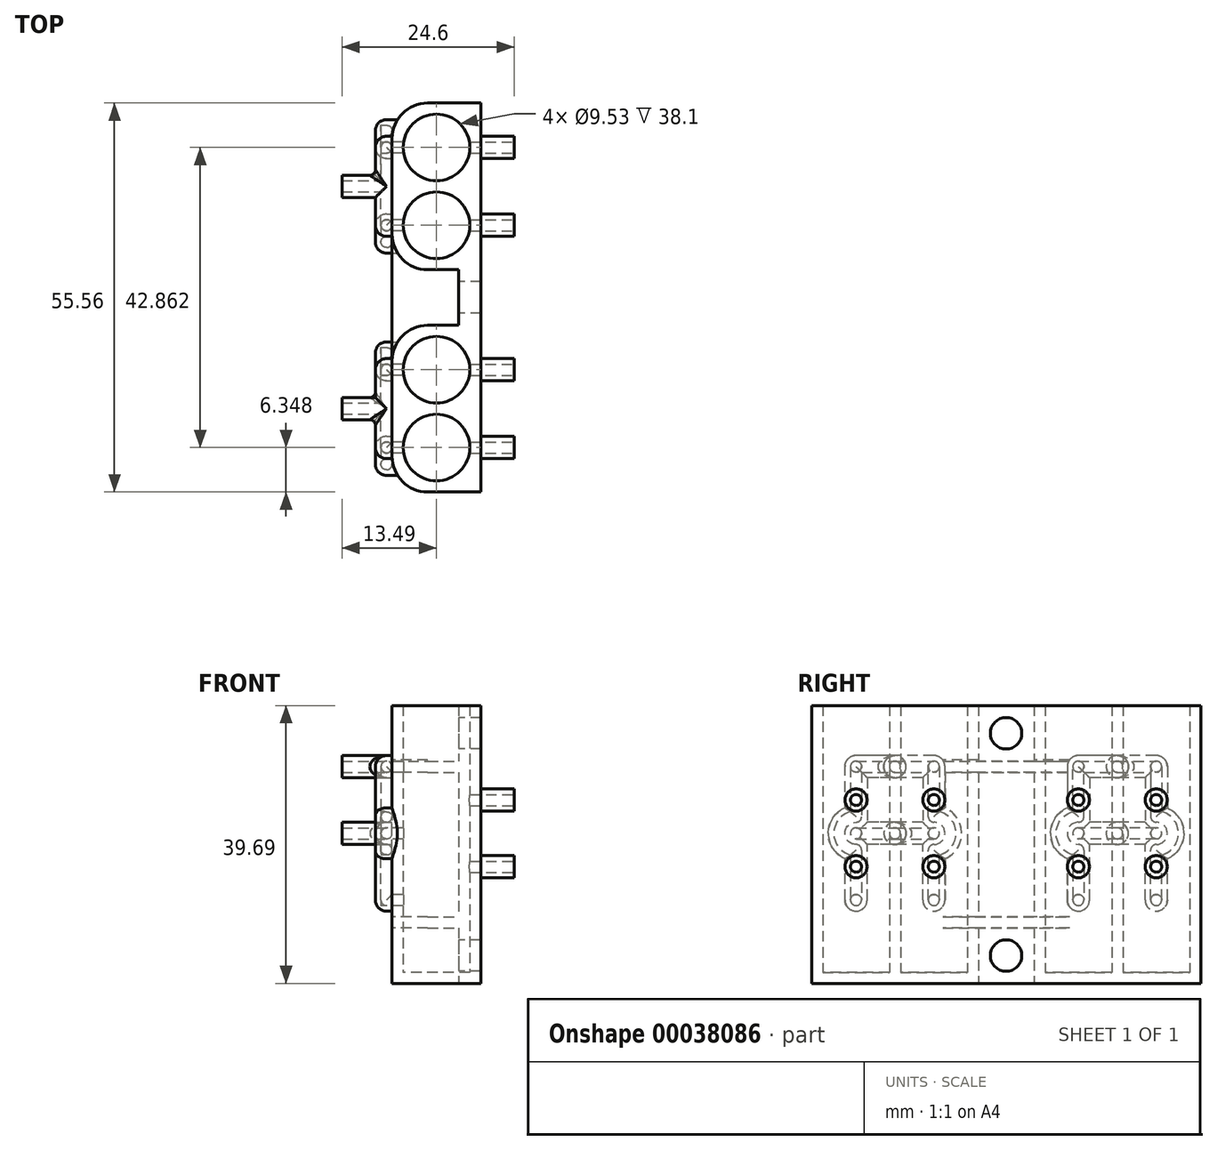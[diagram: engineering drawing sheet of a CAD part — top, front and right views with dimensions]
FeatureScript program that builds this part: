
annotation { "Feature Type Name" : "Feature", "Feature Type Description" : "" }
export const myFeature = defineFeature(function(context is Context, id is Id, definition is map)
    precondition{}
    {
        {
            var Q0;
            Q0=qCreatedBy(makeId("Top.planeOp"),FACE);
            var sketch = newSketch(context, id + "F0", { "sketchPlane" : qUnion([Q0])});
            skLineSegment(sketch, "E0.bottom", {"start": v(0, 0) * mm, "end": v(12.7, 0) * mm});
            skLineSegment(sketch, "E0.top", {"start": v(0, -23.81) * mm, "end": v(9.53, -23.81) * mm});
            skLineSegment(sketch, "E0.left", {"start": v(0, 0) * mm, "end": v(0, -23.81) * mm});
            skLineSegment(sketch, "E0.right", {"start": v(12.7, 0) * mm, "end": v(12.7, -55.56) * mm});
            skLineSegment(sketch, "E1", {"start": v(6.35, 0) * mm, "end": v(6.35, -6.35) * mm, "construction": true});
            skLineSegment(sketch, "E2", {"start": v(6.35, -6.35) * mm, "end": v(6.35, -17.46) * mm, "construction": true});
            skLineSegment(sketch, "E3", {"start": v(6.35, -17.46) * mm, "end": v(6.35, -23.81) * mm, "construction": true});
            skCircle(sketch, "E4", {"center": v(6.35, -17.46) * mm, "radius": 4.76 * mm});
            skCircle(sketch, "E5", {"center": v(6.35, -6.35) * mm, "radius": 4.76 * mm});
            skLineSegment(sketch, "E6", {"start": v(9.53, -23.81) * mm, "end": v(9.53, -31.75) * mm});
            skLineSegment(sketch, "E7.bottom", {"start": v(9.53, -31.75) * mm, "end": v(0, -31.75) * mm});
            skLineSegment(sketch, "E7.top", {"start": v(12.7, -55.56) * mm, "end": v(0, -55.56) * mm});
            skLineSegment(sketch, "E7.right", {"start": v(0, -31.75) * mm, "end": v(0, -55.56) * mm});
            skLineSegment(sketch, "E8", {"start": v(9.53, -27.78) * mm, "end": v(12.7, -27.78) * mm, "construction": true});
            skLineSegment(sketch, "E9", {"start": v(6.35, -31.75) * mm, "end": v(6.35, -38.1) * mm, "construction": true});
            skLineSegment(sketch, "E10", {"start": v(6.35, -38.1) * mm, "end": v(6.35, -49.21) * mm, "construction": true});
            skLineSegment(sketch, "E11", {"start": v(6.35, -49.21) * mm, "end": v(6.35, -55.56) * mm, "construction": true});
            skCircle(sketch, "E12", {"center": v(6.35, -49.21) * mm, "radius": 4.76 * mm});
            skCircle(sketch, "E13", {"center": v(6.35, -38.1) * mm, "radius": 4.76 * mm});
            skSolve(sketch);
        }
        {
            var Q0;
            Q0 = qSketchRegion(id + "F0", true);
            extrude(context, id + "F1", {"entities" : qUnion([Q0]), "depth" : 31.75 * mm});
        }
        {
            var Q0;
            Q0=makeQuery(id+"F1.opExtrude","SWEPT_FACE",FACE,{"disambiguationData":[OSD([sQuery(id+"F0.wireOp",EDGE,"E0.left")])]});
            var sketch = newSketch(context, id + "F2", { "sketchPlane" : qUnion([Q0])});
            skLineSegment(sketch, "E14", {"start": v(17.46, 31.75) * mm, "end": v(17.46, 29.37) * mm, "construction": true});
            skLineSegment(sketch, "E15", {"start": v(6.35, 31.75) * mm, "end": v(6.35, 29.37) * mm, "construction": true});
            skLineSegment(sketch, "E16", {"start": v(17.46, 29.37) * mm, "end": v(17.46, 19.84) * mm, "construction": true});
            skLineSegment(sketch, "E17", {"start": v(17.46, 19.84) * mm, "end": v(17.46, 10.32) * mm, "construction": true});
            skLineSegment(sketch, "E18", {"start": v(6.35, 29.37) * mm, "end": v(6.35, 19.84) * mm, "construction": true});
            skLineSegment(sketch, "E19", {"start": v(6.35, 19.84) * mm, "end": v(6.35, 10.32) * mm, "construction": true});
            skCircle(sketch, "E20", {"center": v(6.35, 10.32) * mm, "radius": 0.8 * mm});
            skCircle(sketch, "E21", {"center": v(6.35, 19.84) * mm, "radius": 0.8 * mm});
            skCircle(sketch, "E22", {"center": v(6.35, 29.37) * mm, "radius": 0.8 * mm});
            skCircle(sketch, "E23", {"center": v(17.46, 29.37) * mm, "radius": 0.8 * mm});
            skCircle(sketch, "E24", {"center": v(17.46, 19.84) * mm, "radius": 0.8 * mm});
            skCircle(sketch, "E25", {"center": v(17.46, 10.32) * mm, "radius": 0.8 * mm});
            skLineSegment(sketch, "E26", {"start": v(38.1, 31.75) * mm, "end": v(38.1, 29.37) * mm, "construction": true});
            skLineSegment(sketch, "E27", {"start": v(38.1, 29.37) * mm, "end": v(38.1, 19.84) * mm, "construction": true});
            skLineSegment(sketch, "E28", {"start": v(38.1, 19.84) * mm, "end": v(38.1, 10.32) * mm, "construction": true});
            skLineSegment(sketch, "E29", {"start": v(49.21, 31.75) * mm, "end": v(49.21, 29.37) * mm, "construction": true});
            skLineSegment(sketch, "E30", {"start": v(49.21, 29.37) * mm, "end": v(49.21, 19.84) * mm, "construction": true});
            skLineSegment(sketch, "E31", {"start": v(49.21, 19.84) * mm, "end": v(49.21, 10.32) * mm, "construction": true});
            skCircle(sketch, "E32", {"center": v(49.21, 10.32) * mm, "radius": 0.8 * mm});
            skCircle(sketch, "E33", {"center": v(49.21, 19.84) * mm, "radius": 0.8 * mm});
            skCircle(sketch, "E34", {"center": v(49.21, 29.37) * mm, "radius": 0.8 * mm});
            skCircle(sketch, "E35", {"center": v(38.1, 29.37) * mm, "radius": 0.8 * mm});
            skCircle(sketch, "E36", {"center": v(38.1, 19.84) * mm, "radius": 0.8 * mm});
            skCircle(sketch, "E37", {"center": v(38.1, 10.32) * mm, "radius": 0.8 * mm});
            skSolve(sketch);
        }
        {
            var Q0;
            Q0 = qSketchRegion(id + "F2", true);
            var Q1;
            Q1=makeQuery(id+"F1.opExtrude","SWEPT_FACE",FACE,{"disambiguationData":[OSD([sQuery(id+"F0.wireOp",EDGE,"E5")])]});
            extrude(context, id + "F3", {"entities" : qUnion([Q0]), "operationType" : NewBodyOperationType.REMOVE, "oppositeDirection" : true, "endBoundEntityFace" : qUnion([Q1]), "depth" : 6.35 * mm});
        }
        {
            var Q0;
            Q0=makeQuery(id+"F1.opExtrude","SWEPT_FACE",FACE,{"disambiguationData":[OSD([sQuery(id+"F0.wireOp",EDGE,"E0.right")])]});
            var sketch = newSketch(context, id + "F4", { "sketchPlane" : qUnion([Q0])});
            skLineSegment(sketch, "E38", {"start": v(-17.46, 29.37) * mm, "end": v(-17.46, 19.84) * mm, "construction": true});
            skLineSegment(sketch, "E39", {"start": v(-17.46, 19.84) * mm, "end": v(-17.46, 10.32) * mm, "construction": true});
            skLineSegment(sketch, "E40", {"start": v(-6.35, 29.37) * mm, "end": v(-6.35, 19.84) * mm, "construction": true});
            skLineSegment(sketch, "E41", {"start": v(-6.35, 19.84) * mm, "end": v(-6.35, 10.32) * mm, "construction": true});
            skCircle(sketch, "E42", {"center": v(-17.46, 24.6) * mm, "radius": 0.8 * mm});
            skCircle(sketch, "E43", {"center": v(-6.35, 24.6) * mm, "radius": 0.8 * mm});
            skCircle(sketch, "E44", {"center": v(-6.35, 15.08) * mm, "radius": 0.8 * mm});
            skCircle(sketch, "E45", {"center": v(-17.46, 15.08) * mm, "radius": 0.8 * mm});
            skLineSegment(sketch, "E46", {"start": v(-38.1, 29.37) * mm, "end": v(-38.1, 19.84) * mm, "construction": true});
            skLineSegment(sketch, "E47", {"start": v(-38.1, 19.84) * mm, "end": v(-38.1, 10.32) * mm, "construction": true});
            skLineSegment(sketch, "E48", {"start": v(-49.21, 29.37) * mm, "end": v(-49.21, 19.84) * mm, "construction": true});
            skLineSegment(sketch, "E49", {"start": v(-49.21, 19.84) * mm, "end": v(-49.21, 10.32) * mm, "construction": true});
            skCircle(sketch, "E50", {"center": v(-38.1, 15.08) * mm, "radius": 0.8 * mm});
            skCircle(sketch, "E51", {"center": v(-49.21, 15.08) * mm, "radius": 0.8 * mm});
            skCircle(sketch, "E52", {"center": v(-49.21, 24.6) * mm, "radius": 0.8 * mm});
            skCircle(sketch, "E53", {"center": v(-38.1, 24.6) * mm, "radius": 0.8 * mm});
            skSolve(sketch);
        }
        {
            var Q0;
            Q0 = qSketchRegion(id + "F4", true);
            var Q1;
            Q1=makeQuery(id+"F1.opExtrude","SWEPT_FACE",FACE,{"disambiguationData":[OSD([sQuery(id+"F0.wireOp",EDGE,"E4")])]});
            extrude(context, id + "F5", {"entities" : qUnion([Q0]), "operationType" : NewBodyOperationType.REMOVE, "oppositeDirection" : true, "endBoundEntityFace" : qUnion([Q1]), "depth" : 6.35 * mm});
        }
        {
            var Q0;
            Q0=makeQuery(id+"F1.opExtrude","SWEPT_FACE",FACE,{"disambiguationData":[OSD([sQuery(id+"F0.wireOp",EDGE,"E0.left")])]});
            var sketch = newSketch(context, id + "F6", { "sketchPlane" : qUnion([Q0])});
            skLineSegment(sketch, "E54.bottom", {"start": v(7.14, 10.32) * mm, "end": v(5.56, 10.32) * mm, "construction": true});
            skLineSegment(sketch, "E54.left", {"start": v(7.14, 10.32) * mm, "end": v(7.14, 17.46) * mm});
            skLineSegment(sketch, "E54.right", {"start": v(5.56, 10.32) * mm, "end": v(5.56, 16.77) * mm});
            skLineSegment(sketch, "E55.left", {"start": v(7.14, 28.58) * mm, "end": v(7.14, 22.23) * mm});
            skLineSegment(sketch, "E55.right", {"start": v(5.56, 29.37) * mm, "end": v(5.56, 22.92) * mm});
            skLineSegment(sketch, "E56.left", {"start": v(18.26, 29.37) * mm, "end": v(18.26, 22.92) * mm});
            skLineSegment(sketch, "E56.right", {"start": v(16.67, 28.57) * mm, "end": v(16.67, 22.22) * mm});
            skLineSegment(sketch, "E57.bottom", {"start": v(18.26, 10.32) * mm, "end": v(16.67, 10.32) * mm, "construction": true});
            skLineSegment(sketch, "E57.left", {"start": v(18.26, 10.32) * mm, "end": v(18.26, 16.77) * mm});
            skLineSegment(sketch, "E57.right", {"start": v(16.67, 10.32) * mm, "end": v(16.67, 17.46) * mm});
            skArc(sketch, "E58", {"start": v(5.56, 10.32) * mm, "mid": v(6.35, 9.53) * mm, "end": v(7.14, 10.32) * mm});
            skArc(sketch, "E59", {"start": v(16.67, 10.32) * mm, "mid": v(17.46, 9.53) * mm, "end": v(18.26, 10.32) * mm});
            skArc(sketch, "E60", {"start": v(18.26, 16.77) * mm, "mid": v(20.64, 19.84) * mm, "end": v(18.26, 22.92) * mm});
            skLineSegment(sketch, "E61", {"start": v(16.67, 10.32) * mm, "end": v(15.88, 10.32) * mm, "construction": true});
            skLineSegment(sketch, "E62", {"start": v(18.26, 10.32) * mm, "end": v(19.05, 10.32) * mm, "construction": true});
            skLineSegment(sketch, "E63", {"start": v(7.14, 10.32) * mm, "end": v(7.94, 10.32) * mm, "construction": true});
            skLineSegment(sketch, "E64", {"start": v(5.56, 10.32) * mm, "end": v(4.76, 10.32) * mm, "construction": true});
            skLineSegment(sketch, "E65", {"start": v(5.56, 29.37) * mm, "end": v(4.76, 29.37) * mm, "construction": true});
            skLineSegment(sketch, "E66", {"start": v(18.26, 29.37) * mm, "end": v(19.05, 29.37) * mm, "construction": true});
            skArc(sketch, "E67", {"start": v(15.88, 10.32) * mm, "mid": v(17.46, 8.73) * mm, "end": v(19.05, 10.32) * mm});
            skArc(sketch, "E68", {"start": v(4.76, 10.32) * mm, "mid": v(6.35, 8.73) * mm, "end": v(7.94, 10.32) * mm});
            skArc(sketch, "E69", {"start": v(5.56, 22.92) * mm, "mid": v(3.18, 19.84) * mm, "end": v(5.56, 16.77) * mm});
            skArc(sketch, "E70", {"start": v(19.05, 16.2) * mm, "mid": v(21.43, 19.84) * mm, "end": v(19.05, 23.48) * mm});
            skLineSegment(sketch, "E71", {"start": v(15.88, 10.32) * mm, "end": v(15.88, 18.26) * mm});
            skLineSegment(sketch, "E72", {"start": v(19.05, 10.32) * mm, "end": v(19.05, 16.2) * mm});
            skLineSegment(sketch, "E73", {"start": v(19.05, 29.37) * mm, "end": v(19.05, 23.48) * mm});
            skLineSegment(sketch, "E74", {"start": v(15.88, 27.78) * mm, "end": v(15.88, 21.43) * mm});
            skLineSegment(sketch, "E75", {"start": v(7.94, 10.32) * mm, "end": v(7.94, 18.26) * mm});
            skLineSegment(sketch, "E76", {"start": v(4.76, 10.32) * mm, "end": v(4.76, 16.2) * mm});
            skLineSegment(sketch, "E77", {"start": v(7.94, 27.78) * mm, "end": v(7.94, 21.43) * mm});
            skLineSegment(sketch, "E78", {"start": v(4.76, 29.37) * mm, "end": v(4.76, 23.48) * mm});
            skArc(sketch, "E79", {"start": v(4.76, 23.48) * mm, "mid": v(2.38, 19.84) * mm, "end": v(4.76, 16.2) * mm});
            skArc(sketch, "E80", {"start": v(6.35, 30.16) * mm, "mid": v(5.79, 29.93) * mm, "end": v(5.56, 29.37) * mm});
            skArc(sketch, "E81", {"start": v(6.35, 30.96) * mm, "mid": v(5.23, 30.5) * mm, "end": v(4.76, 29.37) * mm});
            skLineSegment(sketch, "E82", {"start": v(6.35, 30.16) * mm, "end": v(6.35, 30.96) * mm, "construction": true});
            skLineSegment(sketch, "E83", {"start": v(6.35, 30.16) * mm, "end": v(17.46, 30.16) * mm});
            skLineSegment(sketch, "E84", {"start": v(6.35, 30.96) * mm, "end": v(17.46, 30.96) * mm});
            skArc(sketch, "E85", {"start": v(18.26, 29.37) * mm, "mid": v(18.02, 29.93) * mm, "end": v(17.46, 30.16) * mm});
            skArc(sketch, "E86", {"start": v(19.05, 29.37) * mm, "mid": v(18.59, 30.5) * mm, "end": v(17.46, 30.96) * mm});
            skLineSegment(sketch, "E87", {"start": v(7.14, 28.58) * mm, "end": v(16.67, 28.58) * mm});
            skLineSegment(sketch, "E88", {"start": v(6.35, 29.37) * mm, "end": v(6.35, 28.57) * mm, "construction": true});
            skLineSegment(sketch, "E89", {"start": v(6.35, 28.58) * mm, "end": v(7.14, 28.58) * mm, "construction": true});
            skLineSegment(sketch, "E90", {"start": v(7.94, 27.78) * mm, "end": v(15.88, 27.78) * mm});
            skLineSegment(sketch, "E91", {"start": v(11.9, 28.57) * mm, "end": v(11.9, 27.78) * mm, "construction": true});
            skArc(sketch, "E92", {"start": v(6.35, 21.43) * mm, "mid": v(4.76, 19.84) * mm, "end": v(6.35, 18.26) * mm});
            skLineSegment(sketch, "E93", {"start": v(6.35, 18.26) * mm, "end": v(6.35, 21.43) * mm, "construction": true});
            skArc(sketch, "E94", {"start": v(7.14, 17.46) * mm, "mid": v(6.91, 18.02) * mm, "end": v(6.35, 18.26) * mm});
            skArc(sketch, "E95", {"start": v(6.35, 21.43) * mm, "mid": v(6.91, 21.66) * mm, "end": v(7.14, 22.23) * mm});
            skArc(sketch, "E96", {"start": v(6.35, 20.64) * mm, "mid": v(5.56, 19.84) * mm, "end": v(6.35, 19.05) * mm});
            skLineSegment(sketch, "E97", {"start": v(6.35, 19.05) * mm, "end": v(17.46, 19.05) * mm});
            skLineSegment(sketch, "E98", {"start": v(6.35, 20.64) * mm, "end": v(17.46, 20.64) * mm});
            skLineSegment(sketch, "E99", {"start": v(7.94, 18.26) * mm, "end": v(15.88, 18.26) * mm});
            skLineSegment(sketch, "E100", {"start": v(7.94, 21.43) * mm, "end": v(15.88, 21.43) * mm});
            skArc(sketch, "E101", {"start": v(17.46, 19.05) * mm, "mid": v(18.26, 19.84) * mm, "end": v(17.46, 20.64) * mm});
            skLineSegment(sketch, "E102", {"start": v(17.46, 18.26) * mm, "end": v(17.46, 19.05) * mm, "construction": true});
            skLineSegment(sketch, "E103", {"start": v(17.46, 19.05) * mm, "end": v(17.46, 20.64) * mm, "construction": true});
            skLineSegment(sketch, "E104", {"start": v(17.46, 20.64) * mm, "end": v(17.46, 21.43) * mm, "construction": true});
            skArc(sketch, "E105", {"start": v(17.46, 18.26) * mm, "mid": v(19.05, 19.84) * mm, "end": v(17.46, 21.43) * mm});
            skArc(sketch, "E106", {"start": v(17.46, 18.26) * mm, "mid": v(16.9, 18.02) * mm, "end": v(16.67, 17.46) * mm});
            skArc(sketch, "E107", {"start": v(16.67, 22.22) * mm, "mid": v(16.9, 21.66) * mm, "end": v(17.46, 21.43) * mm});
            skLineSegment(sketch, "E108", {"start": v(11.9, 19.05) * mm, "end": v(11.9, 18.26) * mm, "construction": true});
            skLineSegment(sketch, "E109", {"start": v(11.9, 20.64) * mm, "end": v(11.9, 21.43) * mm, "construction": true});
            skSolve(sketch);
        }
        {
            var Q0;
            Q0 = qSketchRegion(id + "F6", true);
            var Q1;
            Q1=makeQuery(id+"F6.imprint","IMPRINT",FACE,{"disambiguationData":[TD([[makeQuery(id+"F6.imprint","IMPRINT",EDGE,{"derivedFrom":sQuery(id+"F6.wireOp",EDGE,"56f8c796-ba4a-4336-91a6-4f2cd0427d4d")}),-1.0]])]});
            var Q2;
            Q2=makeQuery(id+"F6.imprint","IMPRINT",FACE,{"disambiguationData":[TD([[makeQuery(id+"F6.imprint","IMPRINT",EDGE,{"derivedFrom":sQuery(id+"F6.wireOp",EDGE,"6628252c-3960-42c1-a07d-151ffb62ad8d")}),-1.0]])]});
            extrude(context, id + "F7", {"entities" : qUnion([Q0, Q1, Q2]), "operationType" : NewBodyOperationType.ADD, "depth" : 1.59 * mm});
        }
        {
            var Q0;
            Q0=makeQuery(id+"F7.opExtrude","CAP_FACE",FACE,{"disambiguationData":[OSD([sQuery(id+"F6.wireOp",EDGE,"E54.left"),sQuery(id+"F6.wireOp",EDGE,"E54.right"),sQuery(id+"F6.wireOp",EDGE,"E55.left"),sQuery(id+"F6.wireOp",EDGE,"E55.right"),sQuery(id+"F6.wireOp",EDGE,"E58"),sQuery(id+"F6.wireOp",EDGE,"bc4b8736-4a29-4b48-8581-6a1b7ea78129"),sQuery(id+"F6.wireOp",EDGE,"d77a3df8-c6d6-44c5-9a70-c21e322796ce"),sQuery(id+"F6.wireOp",EDGE,"E68"),sQuery(id+"F6.wireOp",EDGE,"E69"),sQuery(id+"F6.wireOp",EDGE,"0a76e4f2-8457-4cef-829b-78be348e1d2c"),sQuery(id+"F6.wireOp",EDGE,"E75"),sQuery(id+"F6.wireOp",EDGE,"E76"),sQuery(id+"F6.wireOp",EDGE,"E77"),sQuery(id+"F6.wireOp",EDGE,"E78"),sQuery(id+"F6.wireOp",EDGE,"E79"),sQuery(id+"F6.wireOp",EDGE,"1d13e907-3f51-4e45-8cfc-061c8455c8ec")])],"isStart":false});
            var sketch = newSketch(context, id + "F8", { "sketchPlane" : qUnion([Q0])});
            skLineSegment(sketch, "E110.bottom", {"start": v(2.38, 30.96) * mm, "end": v(21.43, 30.96) * mm});
            skLineSegment(sketch, "E110.top", {"start": v(2.38, 8.73) * mm, "end": v(21.43, 8.73) * mm});
            skLineSegment(sketch, "E110.left", {"start": v(2.38, 30.96) * mm, "end": v(2.38, 8.73) * mm});
            skLineSegment(sketch, "E110.right", {"start": v(21.43, 30.96) * mm, "end": v(21.43, 8.73) * mm});
            skLineSegment(sketch, "E111", {"start": v(11.9, 20.64) * mm, "end": v(11.9, 19.05) * mm, "construction": true});
            skLineSegment(sketch, "E112", {"start": v(11.9, 30.16) * mm, "end": v(11.9, 28.58) * mm, "construction": true});
            skCircle(sketch, "E113", {"center": v(11.9, 19.84) * mm, "radius": 0.8 * mm});
            skCircle(sketch, "E114", {"center": v(11.9, 29.37) * mm, "radius": 0.8 * mm});
            skSolve(sketch);
        }
        {
            var Q0;
            Q0=makeQuery(id+"F8.imprint","IMPRINT",FACE,{"disambiguationData":[TD([[makeQuery(id+"F8.imprint","IMPRINT",EDGE,{"derivedFrom":makeQuery(id+"F7.opExtrude","CAP_EDGE",EDGE,{"disambiguationData":[OSD([sQuery(id+"F6.wireOp",EDGE,"E54.left")])],"isStart":false})}),-1.0]])]});
            var Q1;
            Q1=makeQuery(id+"F8.imprint","IMPRINT",FACE,{"disambiguationData":[TD([[makeQuery(id+"F8.imprint","IMPRINT",EDGE,{"derivedFrom":sQuery(id+"F8.wireOp",EDGE,"01027737-762b-4a74-874d-f0db105ad4ae")}),-1.0]])]});
            var Q2;
            Q2=makeQuery(id+"F8.imprint","IMPRINT",FACE,{"disambiguationData":[TD([[makeQuery(id+"F8.imprint","IMPRINT",EDGE,{"derivedFrom":makeQuery(id+"F7.opExtrude","CAP_EDGE",EDGE,{"disambiguationData":[OSD([sQuery(id+"F6.wireOp",EDGE,"E54.left")])],"isStart":false})}),1.0]])]});
            var Q3;
            {var subQ1=makeQuery(id+"F7.opExtrude","CAP_EDGE",EDGE,{"disambiguationData":[OSD([sQuery(id+"F6.wireOp",EDGE,"E97")])],"isStart":false});Q3=makeQuery(id+"F8.imprint","IMPRINT",FACE,{"disambiguationData":[TD([[makeQuery(id+"F8.imprint","IMPRINT",EDGE,{"derivedFrom":subQ1}),1.0]])]});}
            var Q4;
            Q4=makeQuery(id+"F8.imprint","IMPRINT",FACE,{"disambiguationData":[TD([[makeQuery(id+"F8.imprint","IMPRINT",EDGE,{"derivedFrom":makeQuery(id+"F7.opExtrude","CAP_EDGE",EDGE,{"disambiguationData":[OSD([sQuery(id+"F6.wireOp",EDGE,"E56.left")])],"isStart":false})}),-1.0]])]});
            extrude(context, id + "F9", {"entities" : qUnion([Q0, Q1, Q2, Q3, Q4]), "operationType" : NewBodyOperationType.ADD, "depth" : 0.8 * mm});
        }
        {
            var Q0;
            Q0=makeQuery(id+"F1.opExtrude","SWEPT_FACE",FACE,{"disambiguationData":[OSD([sQuery(id+"F0.wireOp",EDGE,"E0.right")])]});
            var sketch = newSketch(context, id + "F10", { "sketchPlane" : qUnion([Q0])});
            skCircle(sketch, "E115", {"center": v(-6.35, 24.6) * mm, "radius": 0.8 * mm});
            skCircle(sketch, "E116", {"center": v(-6.35, 15.08) * mm, "radius": 0.8 * mm});
            skCircle(sketch, "E117", {"center": v(-6.35, 15.08) * mm, "radius": 1.59 * mm});
            skCircle(sketch, "E118", {"center": v(-6.35, 24.6) * mm, "radius": 1.59 * mm});
            skCircle(sketch, "E119", {"center": v(-17.46, 15.08) * mm, "radius": 0.8 * mm});
            skCircle(sketch, "E120", {"center": v(-17.46, 15.08) * mm, "radius": 1.59 * mm});
            skCircle(sketch, "E121", {"center": v(-17.46, 24.6) * mm, "radius": 1.59 * mm});
            skCircle(sketch, "E122", {"center": v(-17.46, 24.6) * mm, "radius": 0.8 * mm});
            skCircle(sketch, "E123", {"center": v(-38.1, 15.08) * mm, "radius": 0.8 * mm});
            skCircle(sketch, "E124", {"center": v(-38.1, 15.08) * mm, "radius": 1.59 * mm});
            skCircle(sketch, "E125", {"center": v(-49.21, 15.08) * mm, "radius": 1.59 * mm});
            skCircle(sketch, "E126", {"center": v(-49.21, 15.08) * mm, "radius": 0.8 * mm});
            skCircle(sketch, "E127", {"center": v(-49.21, 24.6) * mm, "radius": 1.59 * mm});
            skCircle(sketch, "E128", {"center": v(-49.21, 24.6) * mm, "radius": 0.8 * mm});
            skCircle(sketch, "E129", {"center": v(-38.1, 24.6) * mm, "radius": 0.8 * mm});
            skCircle(sketch, "E130", {"center": v(-38.1, 24.6) * mm, "radius": 1.59 * mm});
            skSolve(sketch);
        }
        {
            var Q0;
            Q0 = qSketchRegion(id + "F10", true);
            extrude(context, id + "F11", {"entities" : qUnion([Q0]), "operationType" : NewBodyOperationType.ADD, "depth" : 4.76 * mm});
        }
        {
            var Q0;
            Q0=makeQuery(id+"F1.opExtrude","CAP_FACE",FACE,{"disambiguationData":[OSD([sQuery(id+"F0.wireOp",EDGE,"E0.bottom"),sQuery(id+"F0.wireOp",EDGE,"E0.top"),sQuery(id+"F0.wireOp",EDGE,"E0.left"),sQuery(id+"F0.wireOp",EDGE,"E0.right"),sQuery(id+"F0.wireOp",EDGE,"E4"),sQuery(id+"F0.wireOp",EDGE,"E5")])],"isStart":false});
            extrude(context, id + "F12", {"entities" : qUnion([Q0]), "operationType" : NewBodyOperationType.ADD, "depth" : 6.35 * mm});
        }
        {
            var Q0;
            Q0=makeQuery(id+"F1.opExtrude","CAP_FACE",FACE,{"disambiguationData":[OSD([sQuery(id+"F0.wireOp",EDGE,"E0.bottom"),sQuery(id+"F0.wireOp",EDGE,"E0.top"),sQuery(id+"F0.wireOp",EDGE,"E0.left"),sQuery(id+"F0.wireOp",EDGE,"E0.right"),sQuery(id+"F0.wireOp",EDGE,"E4"),sQuery(id+"F0.wireOp",EDGE,"E5")])],"isStart":true});
            var sketch = newSketch(context, id + "F13", { "sketchPlane" : qUnion([Q0])});
            skLineSegment(sketch, "E131.bottom", {"start": v(0, 0) * mm, "end": v(12.7, 0) * mm});
            skLineSegment(sketch, "E131.top", {"start": v(0, 55.56) * mm, "end": v(12.7, 55.56) * mm});
            skLineSegment(sketch, "E131.right", {"start": v(12.7, 0) * mm, "end": v(12.7, 55.56) * mm});
            skLineSegment(sketch, "E132.bottom", {"start": v(0, 23.81) * mm, "end": v(9.53, 23.81) * mm});
            skLineSegment(sketch, "E132.top", {"start": v(0, 31.75) * mm, "end": v(9.53, 31.75) * mm});
            skLineSegment(sketch, "E132.left", {"start": v(0, 23.81) * mm, "end": v(0, 31.75) * mm, "construction": true});
            skLineSegment(sketch, "E132.right", {"start": v(9.53, 23.81) * mm, "end": v(9.53, 31.75) * mm});
            skLineSegment(sketch, "E133", {"start": v(0, 0) * mm, "end": v(0, 23.81) * mm});
            skLineSegment(sketch, "E134", {"start": v(0, 31.75) * mm, "end": v(0, 55.56) * mm});
            skSolve(sketch);
        }
        {
            var Q0;
            Q0 = qSketchRegion(id + "F13", true);
            extrude(context, id + "F14", {"entities" : qUnion([Q0]), "operationType" : NewBodyOperationType.ADD, "depth" : 1.59 * mm});
        }
        {
            var Q0;
            {var subQ0=sQuery(id+"F0.wireOp",EDGE,"E7.right");Q0=makeQuery(id+"F14.boolean.opBoolean","MERGE",FACE,{"derivedFrom":[makeQuery(id+"F12.boolean.opBoolean","MERGE",FACE,{"derivedFrom":[makeQuery(id+"F1.opExtrude","SWEPT_FACE",FACE,{"disambiguationData":[OSD([subQ0])]}),makeQuery(id+"F12.opExtrude","SWEPT_FACE",FACE,{"disambiguationData":[OSD([subQ0])]})]}),makeQuery(id+"F14.opExtrude","SWEPT_FACE",FACE,{"disambiguationData":[OSD([sQuery(id+"F13.wireOp",EDGE,"E134")])]})]});}
            var sketch = newSketch(context, id + "F15", { "sketchPlane" : qUnion([Q0])});
            skLineSegment(sketch, "E135.bottom", {"start": v(49.21, 19.05) * mm, "end": v(38.1, 19.05) * mm});
            skLineSegment(sketch, "E135.top", {"start": v(49.21, 20.64) * mm, "end": v(38.1, 20.64) * mm});
            skLineSegment(sketch, "E135.left", {"start": v(49.21, 19.05) * mm, "end": v(49.21, 20.64) * mm, "construction": true});
            skLineSegment(sketch, "E135.right", {"start": v(38.1, 19.05) * mm, "end": v(38.1, 20.64) * mm, "construction": true});
            skArc(sketch, "E136", {"start": v(38.1, 20.64) * mm, "mid": v(37.3, 19.84) * mm, "end": v(38.1, 19.05) * mm});
            skArc(sketch, "E137", {"start": v(49.21, 19.05) * mm, "mid": v(50, 19.84) * mm, "end": v(49.21, 20.64) * mm});
            skArc(sketch, "E138", {"start": v(38.1, 21.43) * mm, "mid": v(36.51, 19.84) * mm, "end": v(38.1, 18.26) * mm});
            skArc(sketch, "E139", {"start": v(49.21, 18.26) * mm, "mid": v(50.8, 19.84) * mm, "end": v(49.21, 21.43) * mm});
            skLineSegment(sketch, "E140", {"start": v(38.1, 19.05) * mm, "end": v(38.1, 18.26) * mm, "construction": true});
            skLineSegment(sketch, "E141", {"start": v(38.1, 20.64) * mm, "end": v(38.1, 21.43) * mm, "construction": true});
            skLineSegment(sketch, "E142", {"start": v(49.21, 19.05) * mm, "end": v(49.21, 18.26) * mm, "construction": true});
            skLineSegment(sketch, "E143", {"start": v(49.21, 20.64) * mm, "end": v(49.21, 21.43) * mm, "construction": true});
            skArc(sketch, "E144", {"start": v(48.42, 10.32) * mm, "mid": v(49.21, 9.53) * mm, "end": v(50, 10.32) * mm});
            skArc(sketch, "E145", {"start": v(37.3, 10.32) * mm, "mid": v(38.1, 9.53) * mm, "end": v(38.9, 10.32) * mm});
            skLineSegment(sketch, "E146.bottom", {"start": v(50, 10.32) * mm, "end": v(48.42, 10.32) * mm, "construction": true});
            skLineSegment(sketch, "E146.left", {"start": v(50, 10.32) * mm, "end": v(50, 16.77) * mm});
            skLineSegment(sketch, "E146.right", {"start": v(48.42, 10.32) * mm, "end": v(48.42, 17.46) * mm});
            skLineSegment(sketch, "E147.bottom", {"start": v(38.9, 10.32) * mm, "end": v(37.3, 10.32) * mm, "construction": true});
            skLineSegment(sketch, "E147.left", {"start": v(38.9, 10.32) * mm, "end": v(38.9, 17.46) * mm});
            skLineSegment(sketch, "E147.right", {"start": v(37.3, 10.32) * mm, "end": v(37.3, 16.77) * mm});
            skArc(sketch, "E148", {"start": v(49.21, 18.26) * mm, "mid": v(48.65, 18.02) * mm, "end": v(48.42, 17.46) * mm});
            skArc(sketch, "E149", {"start": v(38.9, 17.46) * mm, "mid": v(38.66, 18.02) * mm, "end": v(38.1, 18.26) * mm});
            skLineSegment(sketch, "E150", {"start": v(48.42, 10.32) * mm, "end": v(47.62, 10.32) * mm, "construction": true});
            skLineSegment(sketch, "E151", {"start": v(38.9, 10.32) * mm, "end": v(39.69, 10.32) * mm, "construction": true});
            skLineSegment(sketch, "E152", {"start": v(37.3, 10.32) * mm, "end": v(36.51, 10.32) * mm, "construction": true});
            skLineSegment(sketch, "E153", {"start": v(50, 10.32) * mm, "end": v(50.8, 10.32) * mm, "construction": true});
            skArc(sketch, "E154", {"start": v(47.62, 10.32) * mm, "mid": v(49.21, 8.73) * mm, "end": v(50.8, 10.32) * mm});
            skArc(sketch, "E155", {"start": v(36.51, 10.32) * mm, "mid": v(38.1, 8.73) * mm, "end": v(39.69, 10.32) * mm});
            skLineSegment(sketch, "E156", {"start": v(47.62, 10.32) * mm, "end": v(47.62, 18.26) * mm});
            skLineSegment(sketch, "E157", {"start": v(39.69, 10.32) * mm, "end": v(39.69, 18.26) * mm});
            skLineSegment(sketch, "E158", {"start": v(39.69, 18.26) * mm, "end": v(47.62, 18.26) * mm});
            skArc(sketch, "E159", {"start": v(50, 16.77) * mm, "mid": v(52.39, 19.84) * mm, "end": v(50, 22.92) * mm});
            skArc(sketch, "E160", {"start": v(37.3, 22.92) * mm, "mid": v(34.93, 19.84) * mm, "end": v(37.3, 16.77) * mm});
            skLineSegment(sketch, "E161", {"start": v(37.3, 19.84) * mm, "end": v(36.51, 19.84) * mm, "construction": true});
            skLineSegment(sketch, "E162", {"start": v(36.51, 19.84) * mm, "end": v(34.93, 19.84) * mm, "construction": true});
            skLineSegment(sketch, "E163", {"start": v(34.93, 19.84) * mm, "end": v(34.13, 19.84) * mm, "construction": true});
            skLineSegment(sketch, "E164", {"start": v(36.51, 10.32) * mm, "end": v(36.51, 16.2) * mm});
            skLineSegment(sketch, "E165", {"start": v(50.8, 10.32) * mm, "end": v(50.8, 16.2) * mm});
            skArc(sketch, "E166", {"start": v(36.51, 23.48) * mm, "mid": v(34.13, 19.84) * mm, "end": v(36.51, 16.2) * mm});
            skArc(sketch, "E167", {"start": v(50.8, 16.2) * mm, "mid": v(53.18, 19.84) * mm, "end": v(50.8, 23.48) * mm});
            skLineSegment(sketch, "E168", {"start": v(37.3, 22.92) * mm, "end": v(37.3, 29.37) * mm});
            skLineSegment(sketch, "E169", {"start": v(36.51, 23.48) * mm, "end": v(36.51, 29.37) * mm});
            skLineSegment(sketch, "E170", {"start": v(38.1, 29.37) * mm, "end": v(38.1, 28.57) * mm, "construction": true});
            skLineSegment(sketch, "E171", {"start": v(38.1, 28.57) * mm, "end": v(38.9, 28.57) * mm, "construction": true});
            skArc(sketch, "E172", {"start": v(38.1, 21.43) * mm, "mid": v(38.66, 21.66) * mm, "end": v(38.9, 22.22) * mm});
            skArc(sketch, "E173", {"start": v(48.42, 22.22) * mm, "mid": v(48.65, 21.66) * mm, "end": v(49.21, 21.43) * mm});
            skLineSegment(sketch, "E174", {"start": v(38.9, 22.22) * mm, "end": v(38.9, 28.57) * mm});
            skLineSegment(sketch, "E175", {"start": v(38.9, 28.57) * mm, "end": v(48.42, 28.57) * mm});
            skLineSegment(sketch, "E176", {"start": v(48.42, 28.57) * mm, "end": v(48.42, 22.22) * mm});
            skLineSegment(sketch, "E177.bottom", {"start": v(39.69, 27.78) * mm, "end": v(47.62, 27.78) * mm});
            skLineSegment(sketch, "E177.top", {"start": v(39.69, 21.43) * mm, "end": v(47.62, 21.43) * mm});
            skLineSegment(sketch, "E177.left", {"start": v(39.69, 27.78) * mm, "end": v(39.69, 21.43) * mm});
            skLineSegment(sketch, "E177.right", {"start": v(47.62, 27.78) * mm, "end": v(47.62, 21.43) * mm});
            skLineSegment(sketch, "E178", {"start": v(50.8, 23.48) * mm, "end": v(50.8, 29.37) * mm});
            skLineSegment(sketch, "E179", {"start": v(38.1, 30.16) * mm, "end": v(49.21, 30.16) * mm});
            skLineSegment(sketch, "E180", {"start": v(38.1, 30.96) * mm, "end": v(49.21, 30.96) * mm});
            skLineSegment(sketch, "E181", {"start": v(43.66, 27.78) * mm, "end": v(43.66, 28.57) * mm, "construction": true});
            skLineSegment(sketch, "E182", {"start": v(43.66, 21.43) * mm, "end": v(43.66, 20.64) * mm, "construction": true});
            skLineSegment(sketch, "E183", {"start": v(39.69, 24.6) * mm, "end": v(38.9, 24.6) * mm, "construction": true});
            skArc(sketch, "E184", {"start": v(38.1, 30.16) * mm, "mid": v(37.54, 29.93) * mm, "end": v(37.3, 29.37) * mm});
            skArc(sketch, "E185", {"start": v(50, 29.37) * mm, "mid": v(49.77, 29.93) * mm, "end": v(49.21, 30.16) * mm});
            skLineSegment(sketch, "E186", {"start": v(50, 22.92) * mm, "end": v(50, 29.37) * mm});
            skArc(sketch, "E187", {"start": v(38.1, 30.96) * mm, "mid": v(36.98, 30.5) * mm, "end": v(36.51, 29.37) * mm});
            skArc(sketch, "E188", {"start": v(50.8, 29.37) * mm, "mid": v(50.34, 30.5) * mm, "end": v(49.21, 30.96) * mm});
            skSolve(sketch);
        }
        {
            var Q0;
            Q0 = qSketchRegion(id + "F15", true);
            extrude(context, id + "F16", {"entities" : qUnion([Q0]), "operationType" : NewBodyOperationType.ADD, "depth" : 1.59 * mm});
        }
        {
            var Q0;
            Q0=makeQuery(id+"F16.opExtrude","CAP_FACE",FACE,{"disambiguationData":[OSD([sQuery(id+"F15.wireOp",EDGE,"E135.bottom"),sQuery(id+"F15.wireOp",EDGE,"E135.top"),sQuery(id+"F15.wireOp",EDGE,"E136"),sQuery(id+"F15.wireOp",EDGE,"E137"),sQuery(id+"F15.wireOp",EDGE,"E138"),sQuery(id+"F15.wireOp",EDGE,"E139"),sQuery(id+"F15.wireOp",EDGE,"E144"),sQuery(id+"F15.wireOp",EDGE,"E145"),sQuery(id+"F15.wireOp",EDGE,"E146.left"),sQuery(id+"F15.wireOp",EDGE,"E146.right"),sQuery(id+"F15.wireOp",EDGE,"E147.left"),sQuery(id+"F15.wireOp",EDGE,"E147.right"),sQuery(id+"F15.wireOp",EDGE,"E148"),sQuery(id+"F15.wireOp",EDGE,"E149"),sQuery(id+"F15.wireOp",EDGE,"E154"),sQuery(id+"F15.wireOp",EDGE,"E155"),sQuery(id+"F15.wireOp",EDGE,"E156"),sQuery(id+"F15.wireOp",EDGE,"E157"),sQuery(id+"F15.wireOp",EDGE,"E158"),sQuery(id+"F15.wireOp",EDGE,"E159"),sQuery(id+"F15.wireOp",EDGE,"E160"),sQuery(id+"F15.wireOp",EDGE,"E164"),sQuery(id+"F15.wireOp",EDGE,"E165"),sQuery(id+"F15.wireOp",EDGE,"E166"),sQuery(id+"F15.wireOp",EDGE,"E167"),sQuery(id+"F15.wireOp",EDGE,"E168"),sQuery(id+"F15.wireOp",EDGE,"E169"),sQuery(id+"F15.wireOp",EDGE,"E172"),sQuery(id+"F15.wireOp",EDGE,"E173"),sQuery(id+"F15.wireOp",EDGE,"E174"),sQuery(id+"F15.wireOp",EDGE,"E175"),sQuery(id+"F15.wireOp",EDGE,"E176"),sQuery(id+"F15.wireOp",EDGE,"E177.bottom"),sQuery(id+"F15.wireOp",EDGE,"E177.top"),sQuery(id+"F15.wireOp",EDGE,"E177.left"),sQuery(id+"F15.wireOp",EDGE,"E177.right"),sQuery(id+"F15.wireOp",EDGE,"E178"),sQuery(id+"F15.wireOp",EDGE,"E179"),sQuery(id+"F15.wireOp",EDGE,"E180"),sQuery(id+"F15.wireOp",EDGE,"E184"),sQuery(id+"F15.wireOp",EDGE,"E185"),sQuery(id+"F15.wireOp",EDGE,"E186"),sQuery(id+"F15.wireOp",EDGE,"E187"),sQuery(id+"F15.wireOp",EDGE,"E188")])],"isStart":false});
            var sketch = newSketch(context, id + "F17", { "sketchPlane" : qUnion([Q0])});
            skLineSegment(sketch, "E189.bottom", {"start": v(34.13, 30.96) * mm, "end": v(53.18, 30.96) * mm});
            skLineSegment(sketch, "E189.top", {"start": v(34.13, 8.73) * mm, "end": v(53.18, 8.73) * mm});
            skLineSegment(sketch, "E189.left", {"start": v(34.13, 30.96) * mm, "end": v(34.13, 8.73) * mm});
            skLineSegment(sketch, "E189.right", {"start": v(53.18, 30.96) * mm, "end": v(53.18, 8.73) * mm});
            skLineSegment(sketch, "E190", {"start": v(38.1, 19.84) * mm, "end": v(49.21, 19.84) * mm, "construction": true});
            skLineSegment(sketch, "E191", {"start": v(38.1, 29.37) * mm, "end": v(49.21, 29.37) * mm, "construction": true});
            skCircle(sketch, "E192", {"center": v(43.66, 29.37) * mm, "radius": 0.8 * mm});
            skCircle(sketch, "E193", {"center": v(43.66, 19.84) * mm, "radius": 0.8 * mm});
            skSolve(sketch);
        }
        {
            var Q0;
            Q0=makeQuery(id+"F17.imprint","IMPRINT",FACE,{"disambiguationData":[TD([[makeQuery(id+"F17.imprint","IMPRINT",EDGE,{"derivedFrom":makeQuery(id+"F16.opExtrude","CAP_EDGE",EDGE,{"disambiguationData":[OSD([sQuery(id+"F15.wireOp",EDGE,"E138")])],"isStart":false})}),-1.0]])]});
            var Q1;
            Q1=makeQuery(id+"F17.imprint","IMPRINT",FACE,{"disambiguationData":[TD([[makeQuery(id+"F17.imprint","IMPRINT",EDGE,{"derivedFrom":makeQuery(id+"F16.opExtrude","CAP_EDGE",EDGE,{"disambiguationData":[OSD([sQuery(id+"F15.wireOp",EDGE,"E139")])],"isStart":false})}),-1.0]])]});
            var Q2;
            {var subQ5=makeQuery(id+"F16.opExtrude","CAP_EDGE",EDGE,{"disambiguationData":[OSD([sQuery(id+"F15.wireOp",EDGE,"E136")])],"isStart":false});Q2=makeQuery(id+"F17.imprint","IMPRINT",FACE,{"disambiguationData":[TD([[makeQuery(id+"F17.imprint","IMPRINT",EDGE,{"derivedFrom":subQ5}),1.0]])]});}
            var Q3;
            {var subQ5=makeQuery(id+"F16.opExtrude","CAP_EDGE",EDGE,{"disambiguationData":[OSD([sQuery(id+"F15.wireOp",EDGE,"E137")])],"isStart":false});Q3=makeQuery(id+"F17.imprint","IMPRINT",FACE,{"disambiguationData":[TD([[makeQuery(id+"F17.imprint","IMPRINT",EDGE,{"derivedFrom":subQ5}),1.0]])]});}
            var Q4;
            {var subQ8=makeQuery(id+"F16.opExtrude","CAP_EDGE",EDGE,{"disambiguationData":[OSD([sQuery(id+"F15.wireOp",EDGE,"E136")])],"isStart":false});Q4=makeQuery(id+"F17.imprint","IMPRINT",FACE,{"disambiguationData":[TD([[makeQuery(id+"F17.imprint","IMPRINT",EDGE,{"derivedFrom":subQ8}),-1.0]])]});}
            var Q5;
            Q5=makeQuery(id+"F9.opExtrude","CAP_FACE",FACE,{"disambiguationData":[OSD([sQuery(id+"F6.wireOp",EDGE,"E67"),sQuery(id+"F6.wireOp",EDGE,"E68"),sQuery(id+"F6.wireOp",EDGE,"E70"),sQuery(id+"F6.wireOp",EDGE,"E71"),sQuery(id+"F6.wireOp",EDGE,"E72"),sQuery(id+"F6.wireOp",EDGE,"E73"),sQuery(id+"F6.wireOp",EDGE,"E74"),sQuery(id+"F6.wireOp",EDGE,"E75"),sQuery(id+"F6.wireOp",EDGE,"E76"),sQuery(id+"F6.wireOp",EDGE,"E77"),sQuery(id+"F6.wireOp",EDGE,"E78"),sQuery(id+"F6.wireOp",EDGE,"E79"),sQuery(id+"F6.wireOp",EDGE,"E81"),sQuery(id+"F6.wireOp",EDGE,"E86"),sQuery(id+"F6.wireOp",EDGE,"E90"),sQuery(id+"F6.wireOp",EDGE,"E99"),sQuery(id+"F6.wireOp",EDGE,"E100"),sQuery(id+"F8.wireOp",EDGE,"E110.bottom"),sQuery(id+"F8.wireOp",EDGE,"E113"),sQuery(id+"F8.wireOp",EDGE,"E114")])],"isStart":false});
            extrude(context, id + "F18", {"entities" : qUnion([Q0, Q1, Q2, Q3, Q4]), "operationType" : NewBodyOperationType.ADD, "endBound" : BoundingType.UP_TO_SURFACE, "endBoundEntityFace" : qUnion([Q5]), "depth" : 25.4 * mm});
        }
        {
            var Q0;
            Q0=makeQuery(id+"F7.opExtrude","CAP_EDGE",EDGE,{"disambiguationData":[OSD([sQuery(id+"F6.wireOp",EDGE,"E69")])],"isStart":true});
            var Q1;
            Q1=makeQuery(id+"F7.opExtrude","CAP_EDGE",EDGE,{"disambiguationData":[OSD([sQuery(id+"F6.wireOp",EDGE,"E54.right")])],"isStart":true});
            var Q2;
            Q2=makeQuery(id+"F7.opExtrude","CAP_EDGE",EDGE,{"disambiguationData":[OSD([sQuery(id+"F6.wireOp",EDGE,"E54.left")])],"isStart":true});
            var Q3;
            Q3=makeQuery(id+"F7.opExtrude","CAP_EDGE",EDGE,{"disambiguationData":[OSD([sQuery(id+"F6.wireOp",EDGE,"0a76e4f2-8457-4cef-829b-78be348e1d2c")])],"isStart":true});
            var Q4;
            Q4=makeQuery(id+"F7.opExtrude","CAP_EDGE",EDGE,{"disambiguationData":[OSD([sQuery(id+"F6.wireOp",EDGE,"fdd66166-4080-40fd-9888-66c6cbb37ced")])],"isStart":true});
            var Q5;
            Q5=makeQuery(id+"F7.opExtrude","CAP_EDGE",EDGE,{"disambiguationData":[OSD([sQuery(id+"F6.wireOp",EDGE,"E55.left")])],"isStart":true});
            var Q6;
            Q6=makeQuery(id+"F7.opExtrude","CAP_EDGE",EDGE,{"disambiguationData":[OSD([sQuery(id+"F6.wireOp",EDGE,"E55.right")])],"isStart":true});
            var Q7;
            Q7=makeQuery(id+"F7.opExtrude","CAP_EDGE",EDGE,{"disambiguationData":[OSD([sQuery(id+"F6.wireOp",EDGE,"E56.right")])],"isStart":true});
            var Q8;
            Q8=makeQuery(id+"F7.opExtrude","CAP_EDGE",EDGE,{"disambiguationData":[OSD([sQuery(id+"F6.wireOp",EDGE,"ee9f118d-7ad8-4186-9314-d135c9a27152")])],"isStart":true});
            var Q9;
            Q9=makeQuery(id+"F7.opExtrude","CAP_EDGE",EDGE,{"disambiguationData":[OSD([sQuery(id+"F6.wireOp",EDGE,"70b7f4d5-55b9-4ed3-b25e-ef224408d947")])],"isStart":true});
            var Q10;
            Q10=makeQuery(id+"F7.opExtrude","CAP_EDGE",EDGE,{"disambiguationData":[OSD([sQuery(id+"F6.wireOp",EDGE,"E56.left")])],"isStart":true});
            var Q11;
            Q11=makeQuery(id+"F7.opExtrude","CAP_EDGE",EDGE,{"disambiguationData":[OSD([sQuery(id+"F6.wireOp",EDGE,"E60")])],"isStart":true});
            var Q12;
            Q12=makeQuery(id+"F7.opExtrude","CAP_EDGE",EDGE,{"disambiguationData":[OSD([sQuery(id+"F6.wireOp",EDGE,"E57.left")])],"isStart":true});
            var Q13;
            Q13=makeQuery(id+"F7.opExtrude","CAP_EDGE",EDGE,{"disambiguationData":[OSD([sQuery(id+"F6.wireOp",EDGE,"E57.right")])],"isStart":true});
            var Q14;
            Q14=makeQuery(id+"F7.opExtrude","CAP_EDGE",EDGE,{"disambiguationData":[OSD([sQuery(id+"F6.wireOp",EDGE,"bc4b8736-4a29-4b48-8581-6a1b7ea78129")])],"isStart":false});
            var Q15;
            Q15=makeQuery(id+"F7.opExtrude","CAP_EDGE",EDGE,{"disambiguationData":[OSD([sQuery(id+"F6.wireOp",EDGE,"E55.left")])],"isStart":false});
            var Q16;
            Q16=makeQuery(id+"F7.opExtrude","CAP_EDGE",EDGE,{"disambiguationData":[OSD([sQuery(id+"F6.wireOp",EDGE,"0a76e4f2-8457-4cef-829b-78be348e1d2c")])],"isStart":false});
            var Q17;
            Q17=makeQuery(id+"F7.opExtrude","CAP_EDGE",EDGE,{"disambiguationData":[OSD([sQuery(id+"F6.wireOp",EDGE,"E69")])],"isStart":false});
            var Q18;
            Q18=makeQuery(id+"F7.opExtrude","CAP_EDGE",EDGE,{"disambiguationData":[OSD([sQuery(id+"F6.wireOp",EDGE,"E54.right")])],"isStart":false});
            var Q19;
            Q19=makeQuery(id+"F7.opExtrude","CAP_EDGE",EDGE,{"disambiguationData":[OSD([sQuery(id+"F6.wireOp",EDGE,"E54.left")])],"isStart":false});
            var Q20;
            Q20=makeQuery(id+"F7.opExtrude","CAP_EDGE",EDGE,{"disambiguationData":[OSD([sQuery(id+"F6.wireOp",EDGE,"fdd66166-4080-40fd-9888-66c6cbb37ced")])],"isStart":false});
            var Q21;
            Q21=makeQuery(id+"F7.opExtrude","CAP_EDGE",EDGE,{"disambiguationData":[OSD([sQuery(id+"F6.wireOp",EDGE,"E57.left")])],"isStart":false});
            var Q22;
            Q22=makeQuery(id+"F7.opExtrude","CAP_EDGE",EDGE,{"disambiguationData":[OSD([sQuery(id+"F6.wireOp",EDGE,"E57.right")])],"isStart":false});
            var Q23;
            Q23=makeQuery(id+"F7.opExtrude","CAP_EDGE",EDGE,{"disambiguationData":[OSD([sQuery(id+"F6.wireOp",EDGE,"ee9f118d-7ad8-4186-9314-d135c9a27152")])],"isStart":false});
            var Q24;
            Q24=makeQuery(id+"F7.opExtrude","CAP_EDGE",EDGE,{"disambiguationData":[OSD([sQuery(id+"F6.wireOp",EDGE,"70b7f4d5-55b9-4ed3-b25e-ef224408d947")])],"isStart":false});
            var Q25;
            Q25=makeQuery(id+"F7.opExtrude","CAP_EDGE",EDGE,{"disambiguationData":[OSD([sQuery(id+"F6.wireOp",EDGE,"E60")])],"isStart":false});
            var Q26;
            Q26=makeQuery(id+"F7.opExtrude","CAP_EDGE",EDGE,{"disambiguationData":[OSD([sQuery(id+"F6.wireOp",EDGE,"E56.left")])],"isStart":false});
            var Q27;
            Q27=makeQuery(id+"F7.opExtrude","CAP_EDGE",EDGE,{"disambiguationData":[OSD([sQuery(id+"F6.wireOp",EDGE,"E97")])],"isStart":false});
            var Q28;
            Q28=makeQuery(id+"F7.opExtrude","CAP_EDGE",EDGE,{"disambiguationData":[OSD([sQuery(id+"F6.wireOp",EDGE,"E98")])],"isStart":false});
            var Q29;
            Q29=makeQuery(id+"F7.opExtrude","CAP_EDGE",EDGE,{"disambiguationData":[OSD([sQuery(id+"F6.wireOp",EDGE,"E83")])],"isStart":false});
            var Q30;
            Q30=makeQuery(id+"F7.opExtrude","CAP_EDGE",EDGE,{"disambiguationData":[OSD([sQuery(id+"F6.wireOp",EDGE,"E87")])],"isStart":false});
            var Q31;
            Q31=makeQuery(id+"F7.opExtrude","CAP_EDGE",EDGE,{"disambiguationData":[OSD([sQuery(id+"F6.wireOp",EDGE,"E55.right")])],"isStart":false});
            var Q32;
            Q32=makeQuery(id+"F7.opExtrude","CAP_EDGE",EDGE,{"disambiguationData":[OSD([sQuery(id+"F6.wireOp",EDGE,"E97")])],"isStart":true});
            var Q33;
            Q33=makeQuery(id+"F7.opExtrude","CAP_EDGE",EDGE,{"disambiguationData":[OSD([sQuery(id+"F6.wireOp",EDGE,"E98")])],"isStart":true});
            var Q34;
            Q34=makeQuery(id+"F7.opExtrude","CAP_EDGE",EDGE,{"disambiguationData":[OSD([sQuery(id+"F6.wireOp",EDGE,"E83")])],"isStart":true});
            var Q35;
            Q35=makeQuery(id+"F7.opExtrude","CAP_EDGE",EDGE,{"disambiguationData":[OSD([sQuery(id+"F6.wireOp",EDGE,"E87")])],"isStart":true});
            var Q36;
            Q36=makeQuery(id+"F16.opExtrude","CAP_EDGE",EDGE,{"disambiguationData":[OSD([sQuery(id+"F15.wireOp",EDGE,"E179")])],"isStart":true});
            var Q37;
            Q37=makeQuery(id+"F16.opExtrude","CAP_EDGE",EDGE,{"disambiguationData":[OSD([sQuery(id+"F15.wireOp",EDGE,"E175")])],"isStart":true});
            var Q38;
            Q38=makeQuery(id+"F16.opExtrude","CAP_EDGE",EDGE,{"disambiguationData":[OSD([sQuery(id+"F15.wireOp",EDGE,"E186")])],"isStart":true});
            var Q39;
            Q39=makeQuery(id+"F16.opExtrude","CAP_EDGE",EDGE,{"disambiguationData":[OSD([sQuery(id+"F15.wireOp",EDGE,"E159")])],"isStart":true});
            var Q40;
            Q40=makeQuery(id+"F16.opExtrude","CAP_EDGE",EDGE,{"disambiguationData":[OSD([sQuery(id+"F15.wireOp",EDGE,"E176")])],"isStart":true});
            var Q41;
            Q41=makeQuery(id+"F16.opExtrude","CAP_EDGE",EDGE,{"disambiguationData":[OSD([sQuery(id+"F15.wireOp",EDGE,"E146.left")])],"isStart":true});
            var Q42;
            Q42=makeQuery(id+"F16.opExtrude","CAP_EDGE",EDGE,{"disambiguationData":[OSD([sQuery(id+"F15.wireOp",EDGE,"E135.top")])],"isStart":true});
            var Q43;
            Q43=makeQuery(id+"F16.opExtrude","CAP_EDGE",EDGE,{"disambiguationData":[OSD([sQuery(id+"F15.wireOp",EDGE,"E135.bottom")])],"isStart":true});
            var Q44;
            Q44=makeQuery(id+"F16.opExtrude","CAP_EDGE",EDGE,{"disambiguationData":[OSD([sQuery(id+"F15.wireOp",EDGE,"E174")])],"isStart":true});
            var Q45;
            Q45=makeQuery(id+"F16.opExtrude","CAP_EDGE",EDGE,{"disambiguationData":[OSD([sQuery(id+"F15.wireOp",EDGE,"E160")])],"isStart":true});
            var Q46;
            Q46=makeQuery(id+"F16.opExtrude","CAP_EDGE",EDGE,{"disambiguationData":[OSD([sQuery(id+"F15.wireOp",EDGE,"E147.right")])],"isStart":true});
            var Q47;
            Q47=makeQuery(id+"F16.opExtrude","CAP_EDGE",EDGE,{"disambiguationData":[OSD([sQuery(id+"F15.wireOp",EDGE,"E168")])],"isStart":true});
            var Q48;
            Q48=makeQuery(id+"F16.opExtrude","CAP_EDGE",EDGE,{"disambiguationData":[OSD([sQuery(id+"F15.wireOp",EDGE,"E159")])],"isStart":false});
            var Q49;
            Q49=makeQuery(id+"F16.opExtrude","CAP_EDGE",EDGE,{"disambiguationData":[OSD([sQuery(id+"F15.wireOp",EDGE,"E186")])],"isStart":false});
            var Q50;
            {var subQ0=sQuery(id+"F15.wireOp",EDGE,"E175");Q50=makeQuery(id+"F18.boolean.opBoolean","SPLIT",EDGE,{"disambiguationData":[TD([makeQuery(id+"F16.opExtrude","SWEPT_FACE",FACE,{"disambiguationData":[OSD([sQuery(id+"F15.wireOp",EDGE,"E176")])]})])],"derivedFrom":makeQuery(id+"F16.opExtrude","CAP_EDGE",EDGE,{"disambiguationData":[OSD([subQ0])],"isStart":false})});}
            var Q51;
            Q51=makeQuery(id+"F16.opExtrude","CAP_EDGE",EDGE,{"disambiguationData":[OSD([sQuery(id+"F15.wireOp",EDGE,"E176")])],"isStart":false});
            var Q52;
            Q52=makeQuery(id+"F16.opExtrude","CAP_EDGE",EDGE,{"disambiguationData":[OSD([sQuery(id+"F15.wireOp",EDGE,"E139")])],"isStart":false});
            var Q53;
            Q53=makeQuery(id+"F16.opExtrude","CAP_EDGE",EDGE,{"disambiguationData":[OSD([sQuery(id+"F15.wireOp",EDGE,"E174")])],"isStart":false});
            var Q54;
            Q54=makeQuery(id+"F16.opExtrude","CAP_EDGE",EDGE,{"disambiguationData":[OSD([sQuery(id+"F15.wireOp",EDGE,"E160")])],"isStart":false});
            var Q55;
            {var subQ1=sQuery(id+"F15.wireOp",EDGE,"E135.bottom");Q55=makeQuery(id+"F18.boolean.opBoolean","SPLIT",EDGE,{"disambiguationData":[TD([makeQuery(id+"F3.boolean.opBoolean","COPY",FACE,{"derivedFrom":makeQuery(id+"F3.opExtrude","SWEPT_FACE",FACE,{"disambiguationData":[OSD([sQuery(id+"F2.wireOp",EDGE,"E36")])]})})])],"derivedFrom":makeQuery(id+"F16.opExtrude","CAP_EDGE",EDGE,{"disambiguationData":[OSD([subQ1])],"isStart":false})});}
            var Q56;
            {var subQ1=sQuery(id+"F15.wireOp",EDGE,"E135.bottom");Q56=makeQuery(id+"F18.boolean.opBoolean","SPLIT",EDGE,{"disambiguationData":[TD([makeQuery(id+"F3.boolean.opBoolean","COPY",FACE,{"derivedFrom":makeQuery(id+"F3.opExtrude","SWEPT_FACE",FACE,{"disambiguationData":[OSD([sQuery(id+"F2.wireOp",EDGE,"E33")])]})})])],"derivedFrom":makeQuery(id+"F16.opExtrude","CAP_EDGE",EDGE,{"disambiguationData":[OSD([subQ1])],"isStart":false})});}
            fillet(context, id + "F19", {"entities" : qUnion([Q0, Q1, Q2, Q3, Q4, Q5, Q6, Q7, Q8, Q9, Q10, Q11, Q12, Q13, Q14, Q15, Q16, Q17, Q18, Q19, Q20, Q21, Q22, Q23, Q24, Q25, Q26, Q27, Q28, Q29, Q30, Q31, Q32, Q33, Q34, Q35, Q36, Q37, Q38, Q39, Q40, Q41, Q42, Q43, Q44, Q45, Q46, Q47, Q48, Q49, Q50, Q51, Q52, Q53, Q54, Q55, Q56]), "radius" : 0.8 * mm, "tangentPropagation" : true, "allowEdgeOverflow" : false});
        }
        {
            var Q0;
            Q0=makeQuery(id+"F18.opExtrude","CAP_FACE",FACE,{"disambiguationData":[OSD([sQuery(id+"F15.wireOp",EDGE,"E154"),sQuery(id+"F15.wireOp",EDGE,"E155"),sQuery(id+"F15.wireOp",EDGE,"E156"),sQuery(id+"F15.wireOp",EDGE,"E157"),sQuery(id+"F15.wireOp",EDGE,"E158"),sQuery(id+"F15.wireOp",EDGE,"E164"),sQuery(id+"F15.wireOp",EDGE,"E165"),sQuery(id+"F15.wireOp",EDGE,"E166"),sQuery(id+"F15.wireOp",EDGE,"E167"),sQuery(id+"F15.wireOp",EDGE,"E169"),sQuery(id+"F15.wireOp",EDGE,"E177.bottom"),sQuery(id+"F15.wireOp",EDGE,"E177.top"),sQuery(id+"F15.wireOp",EDGE,"E177.left"),sQuery(id+"F15.wireOp",EDGE,"E177.right"),sQuery(id+"F15.wireOp",EDGE,"E178"),sQuery(id+"F15.wireOp",EDGE,"E187"),sQuery(id+"F15.wireOp",EDGE,"E188"),sQuery(id+"F17.wireOp",EDGE,"E189.bottom"),sQuery(id+"F17.wireOp",EDGE,"E192"),sQuery(id+"F17.wireOp",EDGE,"E193")])],"isStart":false});
            var sketch = newSketch(context, id + "F20", { "sketchPlane" : qUnion([Q0])});
            skCircle(sketch, "E194", {"center": v(43.66, 19.84) * mm, "radius": 0.8 * mm});
            skCircle(sketch, "E195", {"center": v(43.66, 19.84) * mm, "radius": 1.59 * mm});
            skCircle(sketch, "E196", {"center": v(43.66, 29.37) * mm, "radius": 1.59 * mm});
            skCircle(sketch, "E197", {"center": v(43.66, 29.37) * mm, "radius": 0.8 * mm});
            skCircle(sketch, "E198", {"center": v(11.9, 19.84) * mm, "radius": 0.8 * mm});
            skCircle(sketch, "E199", {"center": v(11.9, 19.84) * mm, "radius": 1.59 * mm});
            skCircle(sketch, "E200", {"center": v(11.9, 29.37) * mm, "radius": 0.8 * mm});
            skCircle(sketch, "E201", {"center": v(11.9, 29.37) * mm, "radius": 1.59 * mm});
            skSolve(sketch);
        }
        {
            var Q0;
            Q0 = qSketchRegion(id + "F20", true);
            extrude(context, id + "F21", {"entities" : qUnion([Q0]), "operationType" : NewBodyOperationType.ADD, "depth" : 4.76 * mm});
        }
        {
            var Q0;
            {var subQ0=sQuery(id+"F15.wireOp",EDGE,"E157");var subQ1=sQuery(id+"F15.wireOp",EDGE,"E158");Q0=makeQuery(id+"F21.boolean.opBoolean","SPLIT",EDGE,{"disambiguationData":[TD([makeQuery(id+"F16.opExtrude","SWEPT_FACE",FACE,{"disambiguationData":[OSD([subQ0])]})])],"derivedFrom":makeQuery(id+"F18.opExtrude","CAP_EDGE",EDGE,{"disambiguationData":[OSD([subQ1])],"isStart":false})});}
            var Q1;
            {var subQ0=sQuery(id+"F15.wireOp",EDGE,"E177.top");var subQ1=sQuery(id+"F15.wireOp",EDGE,"E177.left");Q1=makeQuery(id+"F21.boolean.opBoolean","SPLIT",EDGE,{"disambiguationData":[TD([makeQuery(id+"F16.opExtrude","SWEPT_FACE",FACE,{"disambiguationData":[OSD([subQ1])]})])],"derivedFrom":makeQuery(id+"F18.opExtrude","CAP_EDGE",EDGE,{"disambiguationData":[OSD([subQ0])],"isStart":false})});}
            var Q2;
            {var subQ0=sQuery(id+"F15.wireOp",EDGE,"E156");var subQ1=sQuery(id+"F15.wireOp",EDGE,"E158");Q2=makeQuery(id+"F21.boolean.opBoolean","SPLIT",EDGE,{"disambiguationData":[TD([makeQuery(id+"F16.opExtrude","SWEPT_FACE",FACE,{"disambiguationData":[OSD([subQ0])]})])],"derivedFrom":makeQuery(id+"F18.opExtrude","CAP_EDGE",EDGE,{"disambiguationData":[OSD([subQ1])],"isStart":false})});}
            var Q3;
            {var subQ0=sQuery(id+"F15.wireOp",EDGE,"E177.top");var subQ1=sQuery(id+"F15.wireOp",EDGE,"E177.right");Q3=makeQuery(id+"F21.boolean.opBoolean","SPLIT",EDGE,{"disambiguationData":[TD([makeQuery(id+"F16.opExtrude","SWEPT_FACE",FACE,{"disambiguationData":[OSD([subQ1])]})])],"derivedFrom":makeQuery(id+"F18.opExtrude","CAP_EDGE",EDGE,{"disambiguationData":[OSD([subQ0])],"isStart":false})});}
            var Q4;
            {var subQ0=sQuery(id+"F15.wireOp",EDGE,"E177.right");var subQ1=sQuery(id+"F15.wireOp",EDGE,"E177.bottom");Q4=makeQuery(id+"F21.boolean.opBoolean","SPLIT",EDGE,{"disambiguationData":[TD([makeQuery(id+"F16.opExtrude","SWEPT_FACE",FACE,{"disambiguationData":[OSD([subQ0])]})])],"derivedFrom":makeQuery(id+"F18.opExtrude","CAP_EDGE",EDGE,{"disambiguationData":[OSD([subQ1])],"isStart":false})});}
            var Q5;
            {var subQ0=sQuery(id+"F17.wireOp",EDGE,"E189.bottom");var subQ1=sQuery(id+"F15.wireOp",EDGE,"E188");Q5=makeQuery(id+"F21.boolean.opBoolean","SPLIT",EDGE,{"disambiguationData":[TD([makeQuery(id+"F16.opExtrude","SWEPT_FACE",FACE,{"disambiguationData":[OSD([subQ1])]})])],"derivedFrom":makeQuery(id+"F18.opExtrude","CAP_EDGE",EDGE,{"disambiguationData":[OSD([subQ0])],"isStart":false})});}
            var Q6;
            Q6=makeQuery(id+"F18.opExtrude","CAP_EDGE",EDGE,{"disambiguationData":[OSD([sQuery(id+"F15.wireOp",EDGE,"E166")])],"isStart":false});
            var Q7;
            Q7=makeQuery(id+"F18.opExtrude","CAP_EDGE",EDGE,{"disambiguationData":[OSD([sQuery(id+"F15.wireOp",EDGE,"E164")])],"isStart":false});
            var Q8;
            Q8=makeQuery(id+"F18.opExtrude","CAP_EDGE",EDGE,{"disambiguationData":[OSD([sQuery(id+"F15.wireOp",EDGE,"E157")])],"isStart":false});
            var Q9;
            Q9=makeQuery(id+"F18.opExtrude","CAP_EDGE",EDGE,{"disambiguationData":[OSD([sQuery(id+"F15.wireOp",EDGE,"E177.left")])],"isStart":false});
            var Q10;
            Q10=makeQuery(id+"F18.opExtrude","CAP_EDGE",EDGE,{"disambiguationData":[OSD([sQuery(id+"F15.wireOp",EDGE,"E177.right")])],"isStart":false});
            var Q11;
            Q11=makeQuery(id+"F18.opExtrude","CAP_EDGE",EDGE,{"disambiguationData":[OSD([sQuery(id+"F15.wireOp",EDGE,"E156")])],"isStart":false});
            var Q12;
            Q12=makeQuery(id+"F18.opExtrude","CAP_EDGE",EDGE,{"disambiguationData":[OSD([sQuery(id+"F15.wireOp",EDGE,"E167")])],"isStart":false});
            var Q13;
            Q13=makeQuery(id+"F18.opExtrude","CAP_EDGE",EDGE,{"disambiguationData":[OSD([sQuery(id+"F15.wireOp",EDGE,"E169")])],"isStart":false});
            var Q14;
            {var subQ0=sQuery(id+"F17.wireOp",EDGE,"E189.bottom");var subQ1=sQuery(id+"F15.wireOp",EDGE,"E187");Q14=makeQuery(id+"F21.boolean.opBoolean","SPLIT",EDGE,{"disambiguationData":[TD([makeQuery(id+"F16.opExtrude","SWEPT_FACE",FACE,{"disambiguationData":[OSD([subQ1])]})])],"derivedFrom":makeQuery(id+"F18.opExtrude","CAP_EDGE",EDGE,{"disambiguationData":[OSD([subQ0])],"isStart":false})});}
            var Q15;
            {var subQ0=sQuery(id+"F15.wireOp",EDGE,"E177.left");var subQ1=sQuery(id+"F15.wireOp",EDGE,"E177.bottom");Q15=makeQuery(id+"F21.boolean.opBoolean","SPLIT",EDGE,{"disambiguationData":[TD([makeQuery(id+"F16.opExtrude","SWEPT_FACE",FACE,{"disambiguationData":[OSD([subQ0])]})])],"derivedFrom":makeQuery(id+"F18.opExtrude","CAP_EDGE",EDGE,{"disambiguationData":[OSD([subQ1])],"isStart":false})});}
            var Q16;
            Q16=makeQuery(id+"F9.opExtrude","CAP_EDGE",EDGE,{"disambiguationData":[OSD([sQuery(id+"F6.wireOp",EDGE,"E72")])],"isStart":false});
            var Q17;
            Q17=makeQuery(id+"F9.opExtrude","CAP_EDGE",EDGE,{"disambiguationData":[OSD([sQuery(id+"F6.wireOp",EDGE,"E70")])],"isStart":false});
            var Q18;
            Q18=makeQuery(id+"F9.opExtrude","CAP_EDGE",EDGE,{"disambiguationData":[OSD([sQuery(id+"F6.wireOp",EDGE,"E73")])],"isStart":false});
            var Q19;
            {var subQ0=sQuery(id+"F8.wireOp",EDGE,"E110.bottom");var subQ1=sQuery(id+"F6.wireOp",EDGE,"E86");Q19=makeQuery(id+"F21.boolean.opBoolean","SPLIT",EDGE,{"disambiguationData":[TD([makeQuery(id+"F7.opExtrude","SWEPT_FACE",FACE,{"disambiguationData":[OSD([subQ1])]})])],"derivedFrom":makeQuery(id+"F9.opExtrude","CAP_EDGE",EDGE,{"disambiguationData":[OSD([subQ0])],"isStart":false})});}
            var Q20;
            {var subQ0=sQuery(id+"F6.wireOp",EDGE,"E77");var subQ1=sQuery(id+"F6.wireOp",EDGE,"E90");Q20=makeQuery(id+"F21.boolean.opBoolean","SPLIT",EDGE,{"disambiguationData":[TD([makeQuery(id+"F7.opExtrude","SWEPT_FACE",FACE,{"disambiguationData":[OSD([subQ0])]})])],"derivedFrom":makeQuery(id+"F9.opExtrude","CAP_EDGE",EDGE,{"disambiguationData":[OSD([subQ1])],"isStart":false})});}
            var Q21;
            Q21=makeQuery(id+"F9.opExtrude","CAP_EDGE",EDGE,{"disambiguationData":[OSD([sQuery(id+"F6.wireOp",EDGE,"E77")])],"isStart":false});
            var Q22;
            Q22=makeQuery(id+"F9.opExtrude","CAP_EDGE",EDGE,{"disambiguationData":[OSD([sQuery(id+"F6.wireOp",EDGE,"E79")])],"isStart":false});
            var Q23;
            Q23=makeQuery(id+"F9.opExtrude","CAP_EDGE",EDGE,{"disambiguationData":[OSD([sQuery(id+"F6.wireOp",EDGE,"E76")])],"isStart":false});
            var Q24;
            Q24=makeQuery(id+"F9.opExtrude","CAP_EDGE",EDGE,{"disambiguationData":[OSD([sQuery(id+"F6.wireOp",EDGE,"E75")])],"isStart":false});
            var Q25;
            {var subQ0=sQuery(id+"F6.wireOp",EDGE,"E75");var subQ1=sQuery(id+"F6.wireOp",EDGE,"E99");Q25=makeQuery(id+"F21.boolean.opBoolean","SPLIT",EDGE,{"disambiguationData":[TD([makeQuery(id+"F7.opExtrude","SWEPT_FACE",FACE,{"disambiguationData":[OSD([subQ0])]})])],"derivedFrom":makeQuery(id+"F9.opExtrude","CAP_EDGE",EDGE,{"disambiguationData":[OSD([subQ1])],"isStart":false})});}
            var Q26;
            {var subQ0=sQuery(id+"F6.wireOp",EDGE,"E77");var subQ1=sQuery(id+"F6.wireOp",EDGE,"E100");Q26=makeQuery(id+"F21.boolean.opBoolean","SPLIT",EDGE,{"disambiguationData":[TD([makeQuery(id+"F7.opExtrude","SWEPT_FACE",FACE,{"disambiguationData":[OSD([subQ0])]})])],"derivedFrom":makeQuery(id+"F9.opExtrude","CAP_EDGE",EDGE,{"disambiguationData":[OSD([subQ1])],"isStart":false})});}
            var Q27;
            Q27=makeQuery(id+"F9.opExtrude","CAP_EDGE",EDGE,{"disambiguationData":[OSD([sQuery(id+"F6.wireOp",EDGE,"E74")])],"isStart":false});
            fillet(context, id + "F22", {"entities" : qUnion([Q0, Q1, Q2, Q3, Q4, Q5, Q6, Q7, Q8, Q9, Q10, Q11, Q12, Q13, Q14, Q15, Q16, Q17, Q18, Q19, Q20, Q21, Q22, Q23, Q24, Q25, Q26, Q27]), "radius" : 1.59 * mm, "tangentPropagation" : true, "allowEdgeOverflow" : false});
        }
        {
            var Q0;
            Q0=makeQuery(id+"F21.boolean.opBoolean","SPLIT",EDGE,{"disambiguationData":[OD(0.0)],"derivedFrom":makeQuery(id+"F21.opExtrude","CAP_EDGE",EDGE,{"disambiguationData":[OSD([sQuery(id+"F20.wireOp",EDGE,"E195")])],"isStart":true})});
            var Q1;
            Q1=makeQuery(id+"F21.boolean.opBoolean","SPLIT",EDGE,{"disambiguationData":[OD(0.0)],"derivedFrom":makeQuery(id+"F21.opExtrude","CAP_EDGE",EDGE,{"disambiguationData":[OSD([sQuery(id+"F20.wireOp",EDGE,"E196")])],"isStart":true})});
            var Q2;
            Q2=makeQuery(id+"F21.boolean.opBoolean","SPLIT",EDGE,{"disambiguationData":[OD(0.0)],"derivedFrom":makeQuery(id+"F21.opExtrude","CAP_EDGE",EDGE,{"disambiguationData":[OSD([sQuery(id+"F20.wireOp",EDGE,"E201")])],"isStart":true})});
            var Q3;
            Q3=makeQuery(id+"F21.boolean.opBoolean","SPLIT",EDGE,{"disambiguationData":[OD(0.0)],"derivedFrom":makeQuery(id+"F21.opExtrude","CAP_EDGE",EDGE,{"disambiguationData":[OSD([sQuery(id+"F20.wireOp",EDGE,"E199")])],"isStart":true})});
            var Q4;
            Q4=makeQuery(id+"F11.opExtrude","CAP_EDGE",EDGE,{"disambiguationData":[OSD([sQuery(id+"F10.wireOp",EDGE,"E127")])],"isStart":true});
            var Q5;
            Q5=makeQuery(id+"F11.opExtrude","CAP_EDGE",EDGE,{"disambiguationData":[OSD([sQuery(id+"F10.wireOp",EDGE,"E125")])],"isStart":true});
            var Q6;
            Q6=makeQuery(id+"F11.opExtrude","CAP_EDGE",EDGE,{"disambiguationData":[OSD([sQuery(id+"F10.wireOp",EDGE,"E124")])],"isStart":true});
            var Q7;
            Q7=makeQuery(id+"F11.opExtrude","CAP_EDGE",EDGE,{"disambiguationData":[OSD([sQuery(id+"F10.wireOp",EDGE,"E130")])],"isStart":true});
            var Q8;
            Q8=makeQuery(id+"F11.opExtrude","CAP_EDGE",EDGE,{"disambiguationData":[OSD([sQuery(id+"F10.wireOp",EDGE,"E120")])],"isStart":true});
            var Q9;
            Q9=makeQuery(id+"F11.opExtrude","CAP_EDGE",EDGE,{"disambiguationData":[OSD([sQuery(id+"F10.wireOp",EDGE,"E121")])],"isStart":true});
            var Q10;
            Q10=makeQuery(id+"F11.opExtrude","CAP_EDGE",EDGE,{"disambiguationData":[OSD([sQuery(id+"F10.wireOp",EDGE,"E117")])],"isStart":true});
            var Q11;
            Q11=makeQuery(id+"F11.opExtrude","CAP_EDGE",EDGE,{"disambiguationData":[OSD([sQuery(id+"F10.wireOp",EDGE,"E118")])],"isStart":true});
            var Q12;
            {var subQ0=makeQuery(id+"F21.opExtrude","SWEPT_FACE",FACE,{"disambiguationData":[OSD([sQuery(id+"F20.wireOp",EDGE,"E195")])]});var subQ1=sQuery(id+"F15.wireOp",EDGE,"E157");var subQ2=sQuery(id+"F15.wireOp",EDGE,"E158");Q12=makeQuery(id+"F22.opFillet","BLEND_EDGE",EDGE,{"blendedFrom":[makeQuery(id+"F21.boolean.opBoolean","SPLIT",EDGE,{"disambiguationData":[TD([makeQuery(id+"F16.opExtrude","SWEPT_FACE",FACE,{"disambiguationData":[OSD([subQ1])]})])],"derivedFrom":makeQuery(id+"F18.opExtrude","CAP_EDGE",EDGE,{"disambiguationData":[OSD([subQ2])],"isStart":false})}),subQ0],"blendedInto":[subQ0]});}
            var Q13;
            {var subQ0=makeQuery(id+"F21.opExtrude","SWEPT_FACE",FACE,{"disambiguationData":[OSD([sQuery(id+"F20.wireOp",EDGE,"E199")])]});var subQ1=sQuery(id+"F6.wireOp",EDGE,"E74");var subQ2=sQuery(id+"F6.wireOp",EDGE,"E100");Q13=makeQuery(id+"F22.opFillet","BLEND_EDGE",EDGE,{"blendedFrom":[makeQuery(id+"F21.boolean.opBoolean","SPLIT",EDGE,{"disambiguationData":[TD([makeQuery(id+"F7.opExtrude","SWEPT_FACE",FACE,{"disambiguationData":[OSD([subQ1])]})])],"derivedFrom":makeQuery(id+"F9.opExtrude","CAP_EDGE",EDGE,{"disambiguationData":[OSD([subQ2])],"isStart":false})}),subQ0],"blendedInto":[subQ0]});}
            var Q14;
            {var subQ0=makeQuery(id+"F21.opExtrude","SWEPT_FACE",FACE,{"disambiguationData":[OSD([sQuery(id+"F20.wireOp",EDGE,"E201")])]});var subQ1=sQuery(id+"F6.wireOp",EDGE,"E74");var subQ2=sQuery(id+"F6.wireOp",EDGE,"E90");Q14=makeQuery(id+"F22.opFillet","BLEND_EDGE",EDGE,{"blendedFrom":[makeQuery(id+"F21.boolean.opBoolean","SPLIT",EDGE,{"disambiguationData":[TD([makeQuery(id+"F7.opExtrude","SWEPT_FACE",FACE,{"disambiguationData":[OSD([subQ1])]})])],"derivedFrom":makeQuery(id+"F9.opExtrude","CAP_EDGE",EDGE,{"disambiguationData":[OSD([subQ2])],"isStart":false})}),subQ0],"blendedInto":[subQ0]});}
            var Q15;
            {var subQ0=makeQuery(id+"F21.opExtrude","SWEPT_FACE",FACE,{"disambiguationData":[OSD([sQuery(id+"F20.wireOp",EDGE,"E196")])]});var subQ1=sQuery(id+"F17.wireOp",EDGE,"E189.bottom");var subQ2=sQuery(id+"F15.wireOp",EDGE,"E188");Q15=makeQuery(id+"F22.opFillet","BLEND_EDGE",EDGE,{"blendedFrom":[makeQuery(id+"F21.boolean.opBoolean","SPLIT",EDGE,{"disambiguationData":[TD([makeQuery(id+"F16.opExtrude","SWEPT_FACE",FACE,{"disambiguationData":[OSD([subQ2])]})])],"derivedFrom":makeQuery(id+"F18.opExtrude","CAP_EDGE",EDGE,{"disambiguationData":[OSD([subQ1])],"isStart":false})}),subQ0],"blendedInto":[subQ0]});}
            var Q16;
            {var subQ0=makeQuery(id+"F21.opExtrude","SWEPT_FACE",FACE,{"disambiguationData":[OSD([sQuery(id+"F20.wireOp",EDGE,"E195")])]});var subQ1=sQuery(id+"F15.wireOp",EDGE,"E177.top");var subQ2=sQuery(id+"F15.wireOp",EDGE,"E177.right");Q16=makeQuery(id+"F22.opFillet","BLEND_EDGE",EDGE,{"blendedFrom":[makeQuery(id+"F21.boolean.opBoolean","SPLIT",EDGE,{"disambiguationData":[TD([makeQuery(id+"F16.opExtrude","SWEPT_FACE",FACE,{"disambiguationData":[OSD([subQ2])]})])],"derivedFrom":makeQuery(id+"F18.opExtrude","CAP_EDGE",EDGE,{"disambiguationData":[OSD([subQ1])],"isStart":false})}),subQ0],"blendedInto":[subQ0]});}
            var Q17;
            {var subQ0=makeQuery(id+"F21.opExtrude","SWEPT_FACE",FACE,{"disambiguationData":[OSD([sQuery(id+"F20.wireOp",EDGE,"E196")])]});var subQ1=sQuery(id+"F15.wireOp",EDGE,"E177.left");var subQ2=sQuery(id+"F15.wireOp",EDGE,"E177.bottom");Q17=makeQuery(id+"F22.opFillet","BLEND_EDGE",EDGE,{"blendedFrom":[makeQuery(id+"F21.boolean.opBoolean","SPLIT",EDGE,{"disambiguationData":[TD([makeQuery(id+"F16.opExtrude","SWEPT_FACE",FACE,{"disambiguationData":[OSD([subQ1])]})])],"derivedFrom":makeQuery(id+"F18.opExtrude","CAP_EDGE",EDGE,{"disambiguationData":[OSD([subQ2])],"isStart":false})}),subQ0],"blendedInto":[subQ0]});}
            var Q18;
            {var subQ0=makeQuery(id+"F21.opExtrude","SWEPT_FACE",FACE,{"disambiguationData":[OSD([sQuery(id+"F20.wireOp",EDGE,"E199")])]});var subQ1=sQuery(id+"F6.wireOp",EDGE,"E77");var subQ2=sQuery(id+"F6.wireOp",EDGE,"E100");Q18=makeQuery(id+"F22.opFillet","BLEND_EDGE",EDGE,{"blendedFrom":[makeQuery(id+"F21.boolean.opBoolean","SPLIT",EDGE,{"disambiguationData":[TD([makeQuery(id+"F7.opExtrude","SWEPT_FACE",FACE,{"disambiguationData":[OSD([subQ1])]})])],"derivedFrom":makeQuery(id+"F9.opExtrude","CAP_EDGE",EDGE,{"disambiguationData":[OSD([subQ2])],"isStart":false})}),subQ0],"blendedInto":[subQ0]});}
            var Q19;
            {var subQ0=makeQuery(id+"F21.opExtrude","SWEPT_FACE",FACE,{"disambiguationData":[OSD([sQuery(id+"F20.wireOp",EDGE,"E201")])]});var subQ1=sQuery(id+"F8.wireOp",EDGE,"E110.bottom");var subQ2=sQuery(id+"F6.wireOp",EDGE,"E81");Q19=makeQuery(id+"F22.opFillet","BLEND_EDGE",EDGE,{"blendedFrom":[makeQuery(id+"F21.boolean.opBoolean","SPLIT",EDGE,{"disambiguationData":[TD([makeQuery(id+"F7.opExtrude","SWEPT_FACE",FACE,{"disambiguationData":[OSD([subQ2])]})])],"derivedFrom":makeQuery(id+"F9.opExtrude","CAP_EDGE",EDGE,{"disambiguationData":[OSD([subQ1])],"isStart":false})}),subQ0],"blendedInto":[subQ0]});}
            fillet(context, id + "F23", {"entities" : qUnion([Q0, Q1, Q2, Q3, Q4, Q5, Q6, Q7, Q8, Q9, Q10, Q11, Q12, Q13, Q14, Q15, Q16, Q17, Q18, Q19]), "radius" : 0.8 * mm, "tangentPropagation" : true, "allowEdgeOverflow" : false});
        }
        {
            var Q0;
            {var subQ0=sQuery(id+"F0.wireOp",EDGE,"E6");Q0=makeQuery(id+"F14.boolean.opBoolean","MERGE",FACE,{"derivedFrom":[makeQuery(id+"F12.boolean.opBoolean","MERGE",FACE,{"derivedFrom":[makeQuery(id+"F1.opExtrude","SWEPT_FACE",FACE,{"disambiguationData":[OSD([subQ0])]}),makeQuery(id+"F12.opExtrude","SWEPT_FACE",FACE,{"disambiguationData":[OSD([subQ0])]})]}),makeQuery(id+"F14.opExtrude","SWEPT_FACE",FACE,{"disambiguationData":[OSD([sQuery(id+"F13.wireOp",EDGE,"E132.right")])]})]});}
            var sketch = newSketch(context, id + "F24", { "sketchPlane" : qUnion([Q0])});
            skLineSegment(sketch, "E202", {"start": v(27.78, -1.59) * mm, "end": v(27.78, 2.38) * mm, "construction": true});
            skLineSegment(sketch, "E203", {"start": v(27.78, 38.1) * mm, "end": v(27.78, 34.13) * mm, "construction": true});
            skCircle(sketch, "E204", {"center": v(27.78, 34.13) * mm, "radius": 2.25 * mm});
            skCircle(sketch, "E205", {"center": v(27.78, 2.38) * mm, "radius": 2.25 * mm});
            skSolve(sketch);
        }
        {
            var Q0;
            Q0 = qSketchRegion(id + "F24", true);
            var Q1;
            {var subQ0=sQuery(id+"F0.wireOp",EDGE,"E0.right");Q1=makeQuery(id+"F14.boolean.opBoolean","MERGE",FACE,{"derivedFrom":[makeQuery(id+"F12.boolean.opBoolean","MERGE",FACE,{"derivedFrom":[makeQuery(id+"F1.opExtrude","SWEPT_FACE",FACE,{"disambiguationData":[OSD([subQ0])]}),makeQuery(id+"F12.opExtrude","SWEPT_FACE",FACE,{"disambiguationData":[OSD([subQ0])]})]}),makeQuery(id+"F14.opExtrude","SWEPT_FACE",FACE,{"disambiguationData":[OSD([sQuery(id+"F13.wireOp",EDGE,"E131.right")])]})]});}
            extrude(context, id + "F25", {"entities" : qUnion([Q0]), "operationType" : NewBodyOperationType.REMOVE, "endBound" : BoundingType.UP_TO_SURFACE, "oppositeDirection" : true, "endBoundEntityFace" : qUnion([Q1]), "depth" : 25.4 * mm});
        }
        {
            var Q0;
            {var subQ0=sQuery(id+"F0.wireOp",EDGE,"E6");Q0=makeQuery(id+"F14.boolean.opBoolean","MERGE",FACE,{"derivedFrom":[makeQuery(id+"F12.boolean.opBoolean","MERGE",FACE,{"derivedFrom":[makeQuery(id+"F1.opExtrude","SWEPT_FACE",FACE,{"disambiguationData":[OSD([subQ0])]}),makeQuery(id+"F12.opExtrude","SWEPT_FACE",FACE,{"disambiguationData":[OSD([subQ0])]})]}),makeQuery(id+"F14.opExtrude","SWEPT_FACE",FACE,{"disambiguationData":[OSD([sQuery(id+"F13.wireOp",EDGE,"E132.right")])]})]});}
            var sketch = newSketch(context, id + "F26", { "sketchPlane" : qUnion([Q0])});
            skLineSegment(sketch, "E206.bottom", {"start": v(23.81, 30.16) * mm, "end": v(31.75, 30.16) * mm});
            skLineSegment(sketch, "E206.top", {"start": v(23.81, 28.58) * mm, "end": v(31.75, 28.58) * mm});
            skLineSegment(sketch, "E206.left", {"start": v(23.81, 30.16) * mm, "end": v(23.81, 28.58) * mm});
            skLineSegment(sketch, "E206.right", {"start": v(31.75, 30.16) * mm, "end": v(31.75, 28.58) * mm});
            skLineSegment(sketch, "E207.bottom", {"start": v(23.81, 6.35) * mm, "end": v(31.75, 6.35) * mm});
            skLineSegment(sketch, "E207.top", {"start": v(23.81, 7.94) * mm, "end": v(31.75, 7.94) * mm});
            skLineSegment(sketch, "E207.left", {"start": v(23.81, 6.35) * mm, "end": v(23.81, 7.94) * mm});
            skLineSegment(sketch, "E207.right", {"start": v(31.75, 6.35) * mm, "end": v(31.75, 7.94) * mm});
            skLineSegment(sketch, "E208", {"start": v(27.78, 38.1) * mm, "end": v(27.78, 30.16) * mm, "construction": true});
            skLineSegment(sketch, "E209", {"start": v(27.78, 6.35) * mm, "end": v(27.78, -1.59) * mm, "construction": true});
            skPoint(sketch, "E210", {"position": v(27.78, 34.13) * mm});
            skPoint(sketch, "E211", {"position": v(27.78, 2.38) * mm});
            skSolve(sketch);
        }
        {
            var Q0;
            Q0 = qSketchRegion(id + "F26", true);
            var Q1;
            {var subQ0=sQuery(id+"F0.wireOp",EDGE,"E0.left");var subQ11=sQuery(id+"F0.wireOp",EDGE,"E0.bottom");Q1=makeQuery(id+"F28.opFillet","SPLIT",FACE,{"disambiguationData":[OD(0.0)],"derivedFrom":makeQuery(id+"F14.boolean.opBoolean","MERGE",FACE,{"derivedFrom":[makeQuery(id+"F12.boolean.opBoolean","MERGE",FACE,{"derivedFrom":[makeQuery(id+"F7.boolean.opBoolean","SPLIT",FACE,{"disambiguationData":[TD([makeQuery(id+"F1.opExtrude","SWEPT_FACE",FACE,{"disambiguationData":[OSD([subQ11])]})])],"derivedFrom":makeQuery(id+"F1.opExtrude","SWEPT_FACE",FACE,{"disambiguationData":[OSD([subQ0])]})}),makeQuery(id+"F12.opExtrude","SWEPT_FACE",FACE,{"disambiguationData":[OSD([subQ0])]})]}),makeQuery(id+"F14.opExtrude","SWEPT_FACE",FACE,{"disambiguationData":[OSD([sQuery(id+"F13.wireOp",EDGE,"E133")])]})]})});}
            extrude(context, id + "F27", {"entities" : qUnion([Q0]), "operationType" : NewBodyOperationType.ADD, "endBound" : BoundingType.UP_TO_SURFACE, "endBoundEntityFace" : qUnion([Q1]), "depth" : 25.4 * mm});
        }
        {
            var Q0;
            {var subQ0=sQuery(id+"F0.wireOp",EDGE,"E0.left");var subQ1=sQuery(id+"F0.wireOp",EDGE,"E0.top");Q0=makeQuery(id+"F14.boolean.opBoolean","MERGE",EDGE,{"derivedFrom":[makeQuery(id+"F12.boolean.opBoolean","MERGE",EDGE,{"derivedFrom":[makeQuery(id+"F1.opExtrude","SWEPT_EDGE",EDGE,{"disambiguationData":[OSD([subQ1,subQ0])]}),makeQuery(id+"F12.opExtrude","SWEPT_EDGE",EDGE,{"disambiguationData":[OSD([subQ1,subQ0])]})]}),makeQuery(id+"F14.opExtrude","SWEPT_EDGE",EDGE,{"disambiguationData":[OSD([sQuery(id+"F13.wireOp",EDGE,"E132.bottom"),sQuery(id+"F13.wireOp",EDGE,"E133")])]})]});}
            var Q1;
            {var subQ0=sQuery(id+"F0.wireOp",EDGE,"E0.left");var subQ1=sQuery(id+"F0.wireOp",EDGE,"E0.bottom");Q1=makeQuery(id+"F14.boolean.opBoolean","MERGE",EDGE,{"derivedFrom":[makeQuery(id+"F12.boolean.opBoolean","MERGE",EDGE,{"derivedFrom":[makeQuery(id+"F1.opExtrude","SWEPT_EDGE",EDGE,{"disambiguationData":[OSD([subQ1,subQ0])]}),makeQuery(id+"F12.opExtrude","SWEPT_EDGE",EDGE,{"disambiguationData":[OSD([subQ1,subQ0])]})]}),makeQuery(id+"F14.opExtrude","SWEPT_EDGE",EDGE,{"disambiguationData":[OSD([sQuery(id+"F13.wireOp",EDGE,"E131.bottom"),sQuery(id+"F13.wireOp",EDGE,"E133")])]})]});}
            var Q2;
            {var subQ0=sQuery(id+"F0.wireOp",EDGE,"E7.right");var subQ1=sQuery(id+"F0.wireOp",EDGE,"E7.top");Q2=makeQuery(id+"F14.boolean.opBoolean","MERGE",EDGE,{"derivedFrom":[makeQuery(id+"F12.boolean.opBoolean","MERGE",EDGE,{"derivedFrom":[makeQuery(id+"F1.opExtrude","SWEPT_EDGE",EDGE,{"disambiguationData":[OSD([subQ1,subQ0])]}),makeQuery(id+"F12.opExtrude","SWEPT_EDGE",EDGE,{"disambiguationData":[OSD([subQ1,subQ0])]})]}),makeQuery(id+"F14.opExtrude","SWEPT_EDGE",EDGE,{"disambiguationData":[OSD([sQuery(id+"F13.wireOp",EDGE,"E131.top"),sQuery(id+"F13.wireOp",EDGE,"E134")])]})]});}
            var Q3;
            {var subQ0=sQuery(id+"F0.wireOp",EDGE,"E7.right");var subQ1=sQuery(id+"F0.wireOp",EDGE,"E7.bottom");Q3=makeQuery(id+"F14.boolean.opBoolean","MERGE",EDGE,{"derivedFrom":[makeQuery(id+"F12.boolean.opBoolean","MERGE",EDGE,{"derivedFrom":[makeQuery(id+"F1.opExtrude","SWEPT_EDGE",EDGE,{"disambiguationData":[OSD([subQ1,subQ0])]}),makeQuery(id+"F12.opExtrude","SWEPT_EDGE",EDGE,{"disambiguationData":[OSD([subQ1,subQ0])]})]}),makeQuery(id+"F14.opExtrude","SWEPT_EDGE",EDGE,{"disambiguationData":[OSD([sQuery(id+"F13.wireOp",EDGE,"E132.top"),sQuery(id+"F13.wireOp",EDGE,"E134")])]})]});}
            fillet(context, id + "F28", {"entities" : qUnion([Q0, Q1, Q2, Q3]), "radius" : 5.08 * mm, "tangentPropagation" : true, "allowEdgeOverflow" : false});
        }
    });
